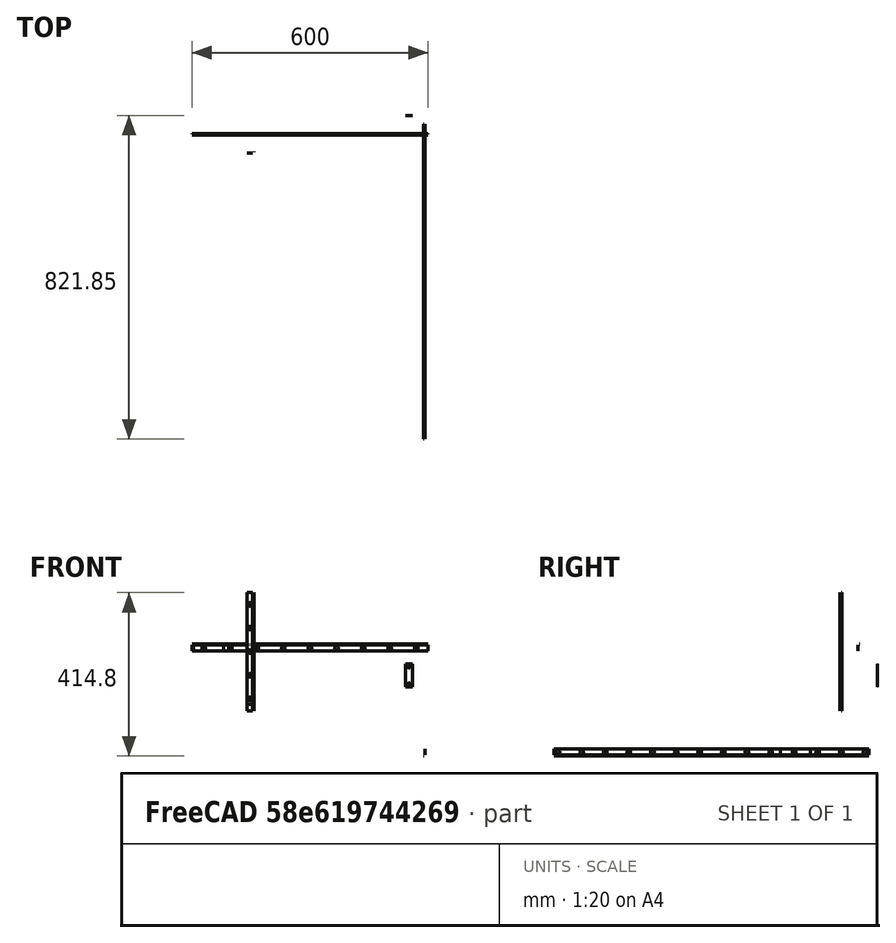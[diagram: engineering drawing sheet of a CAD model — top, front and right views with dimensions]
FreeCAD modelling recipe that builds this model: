
FCSTD DOCUMENT  (FreeCAD 2021.717R24301 +3842 (Git))
Label: 4060CNC
License: Creative Commons Attribution
LicenseURL: http://creativecommons.org/licenses/by/4.0/
objects: App::FeaturePython×31, Part::FeaturePython×21, App::Link×4
note: 20 computed .brp shape members not serialized (recipe doc carries the construction recipe); baked Part::Feature solids carry a one-line shape summary decoded from their .brp
EXTERNAL_REF file=Z-axis.FCStd obj=Assembly
EXTERNAL_REF file=X-axis.FCStd obj=Assembly001
EXTERNAL_REF file=Y-axis.FCStd obj=Assembly
EXTERNAL_REF file=Z-carriage.FCStd obj=Assembly

FEATURE [App::Link] Link  label="Z-axis"
  AutoLinkLabel = true
  AutoPlacement = true
  LinkPlacement = pos=(-190.95,190.1,33.5) rot=(-1e-06,0.707111,-0.707102;0rad)
  LinkedObject = -> <external Z-axis.FCStd>#Assembly
  Placement = pos=(-190.95,190.1,33.5) rot=(-1e-06,0.707111,-0.707102;0rad)
  SyncGroupVisibility = false
  _LinkVersion = 1
FEATURE [App::Link] Link001  label="X-axis"
  AutoLinkLabel = true
  AutoPlacement = true
  LinkPlacement = pos=(15.7,245.5,-55) rot=(0.57735,0.57735,-0.57735;2.0944rad)
  LinkedObject = -> <external X-axis.FCStd>#Assembly001
  Placement = pos=(15.7,245.5,-55) rot=(0.57735,0.57735,-0.57735;2.0944rad)
  SyncGroupVisibility = false
  _LinkVersion = 1
FEATURE [App::Link] Link002  label="Y-axis"
  AutoLinkLabel = true
  AutoPlacement = true
  LinkPlacement = pos=(-233.7,-170,-259.4) rot=(0,0.707107,-0.707107;0rad)
  LinkedObject = -> <external Y-axis.FCStd>#Assembly
  Placement = pos=(-233.7,-170,-259.4) rot=(0,0.707107,-0.707107;0rad)
  SyncGroupVisibility = false
  _LinkVersion = 1
FEATURE [App::Link] Link003  label="Z carriage"
  AutoLinkLabel = true
  AutoPlacement = true
  LinkPlacement = pos=(-278.95,192.85,-22.1) rot=(-5e-06,0.707107,-0.707106;0rad)
  LinkedObject = -> <external Z-carriage.FCStd>#Assembly
  Placement = pos=(-278.95,192.85,-22.1) rot=(-5e-06,0.707107,-0.707106;0rad)
  SyncGroupVisibility = false
  _LinkVersion = 1
FEATURE [Part::FeaturePython] Parts  # WARN: FeaturePython — macro-defined, semantics opaque (R4)
  Group = -> [Link,Link001,Link002,Link003]
  GroupMode = 0
  _LinkVersion = 1
FEATURE [Part::FeaturePython] Assembly  # WARN: FeaturePython — macro-defined, semantics opaque (R4)
  AutoRelax = true
  BuildShape = 0
  Freeze = false
  Group = -> [Constraints,Elements,Parts]
  Verbose = false
  _LinkVersion = 1
  _SolverType = 1
  _Version = 1
FEATURE [App::FeaturePython] Constraints  # WARN: FeaturePython — macro-defined, semantics opaque (R4)
  Group = -> [Constraint001,Constraint002,Constraint003,Constraint004,Constraint005,Constraint,Constraint006,Constraint007,Constraint008,Constraint009]
  _LinkVersion = 1
  _Version = 1
FEATURE [App::FeaturePython] Elements  # WARN: FeaturePython — macro-defined, semantics opaque (R4)
  Group = -> [Element,Element001,Element002,Element003,Element004,Element005,Element006,Element007,Element008,Element009,Element010,Element011,Element012,_Element,_Element001,_Element002,_Element003,_Element004,_Element005]
  _LinkVersion = 1
FEATURE [Part::FeaturePython] Element  label="top-cart-mate@X-axis Assembly"  # link proxy (typed FeaturePython)
  Detach = false
  LinkTransform = true
  LinkedObject = -> Link001 [1.$top-cart-mate@X-beam Assembly.]
  _LinkVersion = 1
  _Parent = -> Elements
FEATURE [Part::FeaturePython] Element001  label="x-top-rail-top-mate@Z-axis assembly"  # link proxy (typed FeaturePython)
  Detach = false
  LinkTransform = true
  LinkedObject = -> Link [1.$x-top-rail-top-mate@HGH20CA-R-Assembly001.]
  _LinkVersion = 1
  _Parent = -> Elements
FEATURE [Part::FeaturePython] Element002  label="x-top-rail-side-mate@Z-axis assembly"  # link proxy (typed FeaturePython)
  Detach = false
  LinkTransform = true
  LinkedObject = -> Link [1.$x-top-rail-side-mate@HGH20CA-R-Assembly001.]
  _LinkVersion = 1
  _Parent = -> Elements
FEATURE [Part::FeaturePython] Element003  label="side-cart-mate@X-axis Assembly"  # link proxy (typed FeaturePython)
  Detach = false
  LinkTransform = true
  LinkedObject = -> Link001 [1.$side-cart-mate@X-beam Assembly.]
  _LinkVersion = 1
  _Parent = -> Elements
FEATURE [App::FeaturePython] Constraint001  label="PlaneAlignment-x-top-rail-cart"  # WARN: FeaturePython — macro-defined, semantics opaque (R4)
  Angle = 0
  AnglePitch = 0
  AngleRoll = 0
  Cascade = false
  Disabled = false
  Group = -> [ElementLink001,ElementLink002]
  LockAngle = false
  _ConstraintType = 37
  _LinkVersion = 1
  _Parent = -> Constraints
FEATURE [App::FeaturePython] ElementLink001  label="top-cart-mate@X-axis Assembly"  # link proxy (typed FeaturePython)
  LinkTransform = true
  LinkedObject = -> Element
  _LinkVersion = 1
  _Parent = -> Constraint001
FEATURE [App::FeaturePython] ElementLink002  label="x-top-rail-top-mate@Z-axis assembly"  # link proxy (typed FeaturePython)
  LinkTransform = true
  LinkedObject = -> Element001
  _LinkVersion = 1
  _Parent = -> Constraint001
FEATURE [App::FeaturePython] Constraint002  label="PlaneAlignment-x-side-rail-cart"  # WARN: FeaturePython — macro-defined, semantics opaque (R4)
  Angle = 0
  AnglePitch = 0
  AngleRoll = 0
  Cascade = false
  Disabled = false
  Group = -> [ElementLink003,ElementLink004]
  LockAngle = false
  _ConstraintType = 37
  _LinkVersion = 1
  _Parent = -> Constraints
FEATURE [App::FeaturePython] ElementLink003  label="side-cart-mate@X-axis Assembly"  # link proxy (typed FeaturePython)
  LinkTransform = true
  LinkedObject = -> Element003
  _LinkVersion = 1
  _Parent = -> Constraint002
FEATURE [App::FeaturePython] ElementLink004  label="x-top-rail-side-mate@Z-axis assembly"  # link proxy (typed FeaturePython)
  LinkTransform = true
  LinkedObject = -> Element002
  _LinkVersion = 1
  _Parent = -> Constraint002
FEATURE [Part::FeaturePython] Element004  label="bf-base@X-axis Assembly"  # link proxy (typed FeaturePython)
  Detach = false
  LinkTransform = true
  LinkedObject = -> Link001 [1.$bf-base@Ballscrew-600-Assembly.]
  _LinkVersion = 1
  _Parent = -> Elements
FEATURE [Part::FeaturePython] Element005  label="x-cart-point@Z-axis assembly"  # link proxy (typed FeaturePython)
  Detach = false
  LinkTransform = true
  LinkedObject = -> Link [1.$x-cart-point@HGH20CA-R-Assembly001.]
  _LinkVersion = 1
  _Parent = -> Elements
FEATURE [Part::FeaturePython] Element006  label="left-point@X-axis Assembly"  # link proxy (typed FeaturePython)
  Detach = false
  LinkTransform = true
  LinkedObject = -> Link001 [1.$left-point@X-beam Assembly.]
  _LinkVersion = 1
  _Parent = -> Elements
FEATURE [App::FeaturePython] Constraint003  label="PointsDistance-X-travel"  # WARN: FeaturePython — macro-defined, semantics opaque (R4)
  Cascade = false
  Disabled = false
  Distance = 80
  Group = -> [ElementLink005,ElementLink006]
  _ConstraintType = 44
  _LinkVersion = 1
  _Parent = -> Constraints
FEATURE [App::FeaturePython] ElementLink005  label="left-point@X-axis Assembly"  # link proxy (typed FeaturePython)
  LinkTransform = true
  LinkedObject = -> Element006
  _LinkVersion = 1
  _Parent = -> Constraint003
FEATURE [App::FeaturePython] ElementLink006  label="x-cart-point@Z-axis assembly"  # link proxy (typed FeaturePython)
  LinkTransform = true
  LinkedObject = -> Element005
  _LinkVersion = 1
  _Parent = -> Constraint003
FEATURE [Part::FeaturePython] Element007  label="top-mate@X-axis Assembly"  # link proxy (typed FeaturePython)
  Detach = false
  LinkTransform = true
  LinkedObject = -> Link001 [1.$top-mate@HGH20CA-R-Assembly.]
  _LinkVersion = 1
  _Parent = -> Elements
FEATURE [Part::FeaturePython] Element008  label="side-mate@X-axis Assembly"  # link proxy (typed FeaturePython)
  Detach = false
  LinkTransform = true
  LinkedObject = -> Link001 [1.$side-mate@HGH20CA-R-Assembly.]
  _LinkVersion = 1
  _Parent = -> Elements
FEATURE [Part::FeaturePython] Element009  label="point@X-axis Assembly"  # link proxy (typed FeaturePython)
  Detach = false
  LinkTransform = true
  LinkedObject = -> Link001 [1.$point@HGH20CA-R-Assembly.]
  _LinkVersion = 1
  _Parent = -> Elements
FEATURE [Part::FeaturePython] Element010  label="side@Base Assembly"  # link proxy (typed FeaturePython)
  Detach = false
  LinkTransform = true
  LinkedObject = -> Link002 [1.$side@HGR20-800 Assembly.]
  _LinkVersion = 1
  _Parent = -> Elements
FEATURE [Part::FeaturePython] Element011  label="point@Base Assembly"  # link proxy (typed FeaturePython)
  Detach = false
  LinkTransform = true
  LinkedObject = -> Link002 [1.$point@HGR20-800 Assembly.]
  _LinkVersion = 1
  _Parent = -> Elements
FEATURE [Part::FeaturePython] Element012  label="top-mate@Base Assembly"  # link proxy (typed FeaturePython)
  Detach = false
  LinkTransform = true
  LinkedObject = -> Link002 [1.$top-mate@HGR20-800 Assembly.]
  _LinkVersion = 1
  _Parent = -> Elements
FEATURE [App::FeaturePython] Constraint004  label="PlaneAlignment-y-top-rail-cart"  # WARN: FeaturePython — macro-defined, semantics opaque (R4)
  Angle = 0
  AnglePitch = 0
  AngleRoll = 0
  Cascade = false
  Disabled = false
  Group = -> [ElementLink007,ElementLink008]
  LockAngle = false
  _ConstraintType = 37
  _LinkVersion = 1
  _Parent = -> Constraints
FEATURE [App::FeaturePython] ElementLink007  label="top-mate@Base Assembly"  # link proxy (typed FeaturePython)
  LinkTransform = true
  LinkedObject = -> Element012
  _LinkVersion = 1
  _Parent = -> Constraint004
FEATURE [App::FeaturePython] ElementLink008  label="top-mate@X-axis Assembly"  # link proxy (typed FeaturePython)
  LinkTransform = true
  LinkedObject = -> Element007
  _LinkVersion = 1
  _Parent = -> Constraint004
FEATURE [App::FeaturePython] Constraint005  label="PlaneAlignment-y-side-rail-cart"  # WARN: FeaturePython — macro-defined, semantics opaque (R4)
  Angle = 0
  AnglePitch = 0
  AngleRoll = 0
  Cascade = false
  Disabled = false
  Group = -> [ElementLink009,ElementLink010]
  LockAngle = false
  _ConstraintType = 37
  _LinkVersion = 1
  _Parent = -> Constraints
FEATURE [App::FeaturePython] ElementLink009  label="side@Base Assembly"  # link proxy (typed FeaturePython)
  LinkTransform = true
  LinkedObject = -> Element010
  _LinkVersion = 1
  _Parent = -> Constraint005
FEATURE [App::FeaturePython] ElementLink010  label="side-mate@X-axis Assembly"  # link proxy (typed FeaturePython)
  LinkTransform = true
  LinkedObject = -> Element008
  _LinkVersion = 1
  _Parent = -> Constraint005
FEATURE [App::FeaturePython] Constraint  label="Locked"  # WARN: FeaturePython — macro-defined, semantics opaque (R4)
  Disabled = false
  Group = -> [ElementLink]
  _ConstraintType = 0
  _LinkVersion = 1
  _Parent = -> Constraints
FEATURE [App::FeaturePython] ElementLink  label="top-mate@Base Assembly"  # link proxy (typed FeaturePython)
  LinkTransform = true
  LinkedObject = -> Element012
  _LinkVersion = 1
  _Parent = -> Constraint
FEATURE [App::FeaturePython] Constraint006  label="PointsDistance-Y-travel"  # WARN: FeaturePython — macro-defined, semantics opaque (R4)
  Cascade = false
  Disabled = false
  Distance = 575
  Group = -> [ElementLink011,ElementLink012]
  _ConstraintType = 44
  _LinkVersion = 1
  _Parent = -> Constraints
FEATURE [App::FeaturePython] ElementLink011  label="point@Base Assembly"  # link proxy (typed FeaturePython)
  LinkTransform = true
  LinkedObject = -> Element011
  _LinkVersion = 1
  _Parent = -> Constraint006
FEATURE [App::FeaturePython] ElementLink012  label="point@X-axis Assembly"  # link proxy (typed FeaturePython)
  LinkTransform = true
  LinkedObject = -> Element009
  _LinkVersion = 1
  _Parent = -> Constraint006
FEATURE [App::FeaturePython] Constraint007  label="PlaneAlignment-z-top-rail-cart"  # WARN: FeaturePython — macro-defined, semantics opaque (R4)
  Angle = 0
  AnglePitch = 0
  AngleRoll = 0
  Cascade = false
  Disabled = false
  Group = -> [ElementLink013,ElementLink014]
  LockAngle = false
  _ConstraintType = 37
  _LinkVersion = 1
  _Parent = -> Constraints
FEATURE [App::FeaturePython] ElementLink013  label="top-mate@Z-axis assembly"  # link proxy (typed FeaturePython)
  LinkTransform = true
  LinkedObject = -> _Element
  _LinkVersion = 1
  _Parent = -> Constraint007
FEATURE [Part::FeaturePython] _Element  label="top-mate@Z-axis assembly"  # link proxy (typed FeaturePython)
  Detach = false
  LinkTransform = true
  LinkedObject = -> Link [1.$top-mate@HGR20-300-Assembly.]
  _LinkVersion = 1
  _Parent = -> Elements
FEATURE [App::FeaturePython] ElementLink014  label="top-mate@Z carriage Assembly"  # link proxy (typed FeaturePython)
  LinkTransform = true
  LinkedObject = -> _Element001
  _LinkVersion = 1
  _Parent = -> Constraint007
FEATURE [Part::FeaturePython] _Element001  label="top-mate@Z carriage Assembly"  # link proxy (typed FeaturePython)
  Detach = false
  LinkTransform = true
  LinkedObject = -> Link003 [1.$top-mate@HGH20CA-R-Assembly.]
  _LinkVersion = 1
  _Parent = -> Elements
FEATURE [App::FeaturePython] Constraint008  label="PlaneAlignment-z-side-rail-cart"  # WARN: FeaturePython — macro-defined, semantics opaque (R4)
  Angle = 0
  AnglePitch = 0
  AngleRoll = 0
  Cascade = false
  Disabled = false
  Group = -> [ElementLink015,ElementLink016]
  LockAngle = false
  _ConstraintType = 37
  _LinkVersion = 1
  _Parent = -> Constraints
FEATURE [App::FeaturePython] ElementLink015  label="r-mate@Z-axis assembly"  # link proxy (typed FeaturePython)
  LinkTransform = true
  LinkedObject = -> _Element002
  _LinkVersion = 1
  _Parent = -> Constraint008
FEATURE [Part::FeaturePython] _Element002  label="r-mate@Z-axis assembly"  # link proxy (typed FeaturePython)
  Detach = false
  LinkTransform = true
  LinkedObject = -> Link [1.$r-mate@HGR20-300-Assembly.]
  _LinkVersion = 1
  _Parent = -> Elements
FEATURE [App::FeaturePython] ElementLink016  label="side-mate@Z carriage Assembly"  # link proxy (typed FeaturePython)
  LinkTransform = true
  LinkedObject = -> _Element003
  _LinkVersion = 1
  _Parent = -> Constraint008
FEATURE [Part::FeaturePython] _Element003  label="side-mate@Z carriage Assembly"  # link proxy (typed FeaturePython)
  Detach = false
  LinkTransform = true
  LinkedObject = -> Link003 [1.$side-mate@HGH20CA-R-Assembly.]
  _LinkVersion = 1
  _Parent = -> Elements
FEATURE [App::FeaturePython] Constraint009  label="PointsDistance-Z-travel"  # WARN: FeaturePython — macro-defined, semantics opaque (R4)
  Cascade = false
  Disabled = false
  Distance = 16
  Group = -> [ElementLink017,ElementLink018]
  _ConstraintType = 44
  _LinkVersion = 1
  _Parent = -> Constraints
FEATURE [App::FeaturePython] ElementLink017  label="point@Z-axis assembly"  # link proxy (typed FeaturePython)
  LinkTransform = true
  LinkedObject = -> _Element004
  _LinkVersion = 1
  _Parent = -> Constraint009
FEATURE [Part::FeaturePython] _Element004  label="point@Z-axis assembly"  # link proxy (typed FeaturePython)
  Detach = false
  LinkTransform = true
  LinkedObject = -> Link [1.$point@HGR20-300-Assembly.]
  _LinkVersion = 1
  _Parent = -> Elements
FEATURE [App::FeaturePython] ElementLink018  label="point@Z carriage Assembly"  # link proxy (typed FeaturePython)
  LinkTransform = true
  LinkedObject = -> _Element005
  _LinkVersion = 1
  _Parent = -> Constraint009
FEATURE [Part::FeaturePython] _Element005  label="point@Z carriage Assembly"  # link proxy (typed FeaturePython)
  Detach = false
  LinkTransform = true
  LinkedObject = -> Link003 [1.$point@HGH20CA-R-Assembly.]
  _LinkVersion = 1
  _Parent = -> Elements

RESOLVED EXTERNAL PARTS (link-assembly join: the EXTERNAL_REF files above that resolve inside this repo's crawl, each included once):
---- part X-axis.FCStd = doc fcstd_a2c1d80cc1b0 ----
FCSTD DOCUMENT  (FreeCAD 2021.717R24301 +3842 (Git))
Label: X-axis
License: Creative Commons Attribution
LicenseURL: http://creativecommons.org/licenses/by/4.0/
objects: App::FeaturePython×78, Part::FeaturePython×72, App::Link×20, App::LinkElement×4, App::DocumentObjectGroup×1
note: 69 computed .brp shape members not serialized (recipe doc carries the construction recipe); baked Part::Feature solids carry a one-line shape summary decoded from their .brp
EXTERNAL_REF file=parts/HGR20.FCStd obj=Assembly001
EXTERNAL_REF file=parts/X axis plates.FCStd obj=Assembly001
EXTERNAL_REF file=parts/X axis plates.FCStd obj=Assembly
EXTERNAL_REF file=parts/Ballscrew.FCStd obj=Assembly003
EXTERNAL_REF file=parts/NEMA23-76.FCStd obj=Assembly001
EXTERNAL_REF file=parts/NEMA23-76.FCStd obj=Assembly
EXTERNAL_REF file=parts/X axis plates.FCStd obj=Assembly003
EXTERNAL_REF file=parts/HGH20CA.FCStd obj=Assembly
EXTERNAL_REF file=parts/HGH20CA.FCStd obj=Assembly001
EXTERNAL_REF file=parts/BallNut.FCStd obj=Assembly
EXTERNAL_REF file=parts/X axis plates.FCStd obj=Assembly005
EXTERNAL_REF file=parts/Extrusion.FCStd obj=Body001
EXTERNAL_REF file=parts/LimitSensor.FCStd obj=Assembly

FEATURE [App::Link] Link  label="HGR20-600"
  AutoLinkLabel = true
  AutoPlacement = true
  LinkPlacement = pos=(-97.7,1.41e-14,25.4) rot=(0,0,1;0rad)
  LinkedObject = -> <external parts/HGR20.FCStd>#Assembly001
  Placement = pos=(-97.7,1.41e-14,25.4) rot=(0,0,1;0rad)
  SyncGroupVisibility = false
  _LinkVersion = 1
FEATURE [App::Link] Link002  label="Top beam"
  AutoLinkLabel = true
  AutoPlacement = true
  LinkedObject = -> Assembly
  SyncGroupVisibility = false
  _LinkVersion = 1
FEATURE [App::Link] Link003  label="Bottom beam"
  AutoLinkLabel = true
  AutoPlacement = true
  LinkPlacement = pos=(-55.7,-2.274e-13,1.776e-13) rot=(0,0,-1;3.14159rad)
  LinkedObject = -> Assembly
  Placement = pos=(-55.7,-2.274e-13,1.776e-13) rot=(0,0,-1;3.14159rad)
  SyncGroupVisibility = false
  _LinkVersion = 1
FEATURE [App::Link] Link004  label="Left plate"
  AutoLinkLabel = true
  AutoPlacement = true
  LinkPlacement = pos=(166.3,-323.85,58.6) rot=(0,1,0;4.71239rad)
  LinkedObject = -> <external parts/X axis plates.FCStd>#Assembly001
  Placement = pos=(166.3,-323.85,58.6) rot=(0,1,0;4.71239rad)
  SyncGroupVisibility = false
  _LinkVersion = 1
FEATURE [App::Link] Link005  label="Right plate"
  AutoLinkLabel = true
  AutoPlacement = true
  LinkPlacement = pos=(166.3,69.85,58.6) rot=(0,1,0;4.71239rad)
  LinkedObject = -> <external parts/X axis plates.FCStd>#Assembly
  Placement = pos=(166.3,69.85,58.6) rot=(0,1,0;4.71239rad)
  SyncGroupVisibility = false
  _LinkVersion = 1
FEATURE [App::Link] Link006  label="Ballscrew-600"
  AutoLinkLabel = true
  AutoPlacement = true
  LinkPlacement = pos=(-27.85,251.9,-6.35) rot=(0,0,-1;3.14159rad)
  LinkedObject = -> <external parts/Ballscrew.FCStd>#Assembly003
  Placement = pos=(-27.85,251.9,-6.35) rot=(0,0,-1;3.14159rad)
  SyncGroupVisibility = false
  _LinkVersion = 1
FEATURE [App::Link] Link007  label="Coupling"
  AutoLinkLabel = true
  AutoPlacement = true
  LinkPlacement = pos=(-27.85,-296.25,18.65) rot=(-0.57735,-0.57735,-0.57735;2.0944rad)
  LinkedObject = -> <external parts/NEMA23-76.FCStd>#Assembly001
  Placement = pos=(-27.85,-296.25,18.65) rot=(-0.57735,-0.57735,-0.57735;2.0944rad)
  SyncGroupVisibility = false
  _LinkVersion = 1
FEATURE [App::Link] Link008  label="NEMA23-76"
  AutoLinkLabel = true
  AutoPlacement = true
  LinkPlacement = pos=(-27.85,-323.85,18.65) rot=(0.57735,-0.57735,0.57735;2.0944rad)
  LinkedObject = -> <external parts/NEMA23-76.FCStd>#Assembly
  Placement = pos=(-27.85,-323.85,18.65) rot=(0.57735,-0.57735,0.57735;2.0944rad)
  SyncGroupVisibility = false
  _LinkVersion = 1
FEATURE [App::Link] Link009  label="Rear plate"
  AutoLinkLabel = true
  AutoPlacement = true
  LinkPlacement = pos=(209.15,-76,-12.7) rot=(0,1,0;4.71239rad)
  LinkedObject = -> <external parts/X axis plates.FCStd>#Assembly003
  Placement = pos=(209.15,-76,-12.7) rot=(0,1,0;4.71239rad)
  SyncGroupVisibility = false
  _LinkVersion = 1
FEATURE [App::Link] Link012  label="HGH20CA-L-L"
  AutoLinkLabel = true
  AutoPlacement = true
  LinkPlacement = pos=(166.3,-274.8,202.6) rot=(-1,0,0;4.71239rad)
  LinkedObject = -> <external parts/HGH20CA.FCStd>#Assembly
  Placement = pos=(166.3,-274.8,202.6) rot=(-1,0,0;4.71239rad)
  SyncGroupVisibility = false
  _LinkVersion = 1
FEATURE [App::Link] Link013  label="HGH20CA-L-R"
  AutoLinkLabel = true
  AutoPlacement = true
  LinkPlacement = pos=(166.3,-274.8,58.6) rot=(-1,0,0;4.71239rad)
  LinkedObject = -> <external parts/HGH20CA.FCStd>#Assembly001
  Placement = pos=(166.3,-274.8,58.6) rot=(-1,0,0;4.71239rad)
  SyncGroupVisibility = false
  _LinkVersion = 1
FEATURE [App::Link] Link014  label="HGH20CA-R-L"
  AutoLinkLabel = true
  AutoPlacement = true
  LinkPlacement = pos=(166.3,274.8,58.6) rot=(1,0,0;4.71239rad)
  LinkedObject = -> Link012
  Placement = pos=(166.3,274.8,58.6) rot=(1,0,0;4.71239rad)
  SyncGroupVisibility = false
  _LinkVersion = 1
FEATURE [App::Link] Link015  label="HGH20CA-R-R"
  AutoLinkLabel = true
  AutoPlacement = true
  LinkPlacement = pos=(166.3,274.8,202.6) rot=(1,0,0;4.71239rad)
  LinkedObject = -> Link013
  Placement = pos=(166.3,274.8,202.6) rot=(1,0,0;4.71239rad)
  SyncGroupVisibility = false
  _LinkVersion = 1
FEATURE [App::Link] Link020  label="Left nut"
  AutoLinkLabel = true
  AutoPlacement = true
  LinkPlacement = pos=(219.3,-305.675,131.475) rot=(0,0.707107,0.707107;3.14159rad)
  LinkedObject = -> <external parts/BallNut.FCStd>#Assembly
  Placement = pos=(219.3,-305.675,131.475) rot=(0,0.707107,0.707107;3.14159rad)
  SyncGroupVisibility = false
  _LinkVersion = 1
FEATURE [App::Link] Link021  label="Right nut"
  AutoLinkLabel = true
  AutoPlacement = true
  LinkPlacement = pos=(219.3,305.675,131.475) rot=(1,0,0;1.5708rad)
  LinkedObject = -> <external parts/BallNut.FCStd>#Assembly
  Placement = pos=(219.3,305.675,131.475) rot=(1,0,0;1.5708rad)
  SyncGroupVisibility = false
  _LinkVersion = 1
FEATURE [App::Link] Link022  label="Gouverner left"
  AutoLinkLabel = true
  AutoPlacement = true
  LinkPlacement = pos=(166.3,-323.85,130.6) rot=(0,1,0;4.71239rad)
  LinkedObject = -> <external parts/X axis plates.FCStd>#Assembly005
  Placement = pos=(166.3,-323.85,130.6) rot=(0,1,0;4.71239rad)
  SyncGroupVisibility = false
  _LinkVersion = 1
FEATURE [App::Link] Link023  label="Gouverner right"
  AutoLinkLabel = true
  AutoPlacement = true
  LinkPlacement = pos=(166.3,323.85,130.6) rot=(0.707107,0,-0.707107;3.14159rad)
  LinkedObject = -> <external parts/X axis plates.FCStd>#Assembly005
  Placement = pos=(166.3,323.85,130.6) rot=(0.707107,0,-0.707107;3.14159rad)
  SyncGroupVisibility = false
  _LinkVersion = 1
FEATURE [App::Link] Link024  label="Extrusion"
  AutoLinkLabel = true
  AutoPlacement = true
  LinkPlacement = pos=(-85,0,0) rot=(0,0,1;0rad)
  LinkedObject = -> <external parts/Extrusion.FCStd>#Body001
  Placement = pos=(-85,0,0) rot=(0,0,1;0rad)
  SyncGroupVisibility = false
  _LinkVersion = 1
FEATURE [Part::FeaturePython] Washer  label="1/4in-Washer"  # Fasteners workbench fastener (typed FeaturePython)
  Placement = pos=(0,0,-1.6002) rot=(0,0,1;0rad)
  diameter = 11
  invert = false
  matchOuter = false
  offset = 0
  type = 1
FEATURE [Part::FeaturePython] Screw  label="1/4inx1/2in-Screw"  # Fasteners workbench fastener (typed FeaturePython)
  diameter = 11
  invert = false
  length = 4
  lengthCustom = 12.7
  matchOuter = false
  offset = 0
  thread = false
  type = 4
FEATURE [Part::FeaturePython] Parts002  # WARN: FeaturePython — macro-defined, semantics opaque (R4)
  Group = -> [Washer,Screw]
  GroupMode = 0
  _LinkVersion = 1
FEATURE [App::LinkElement] Link025_i0
  LinkPlacement = pos=(-63.4102,-234.8,-12.7) rot=(-0.57735,-0.57735,0.57735;2.0944rad)
  LinkedObject = -> Assembly002
  Placement = pos=(-63.4102,-234.8,-12.7) rot=(-0.57735,-0.57735,0.57735;2.0944rad)
  _LinkVersion = 1
FEATURE [App::LinkElement] Link025_i1
  LinkPlacement = pos=(-63.4102,-78.2667,-12.7) rot=(-0.57735,-0.57735,0.57735;2.0944rad)
  LinkedObject = -> Assembly002
  Placement = pos=(-63.4102,-78.2667,-12.7) rot=(-0.57735,-0.57735,0.57735;2.0944rad)
  _LinkVersion = 1
FEATURE [App::LinkElement] Link025_i2
  LinkPlacement = pos=(-63.4102,78.2667,-12.7) rot=(-0.57735,-0.57735,0.57735;2.0944rad)
  LinkedObject = -> Assembly002
  Placement = pos=(-63.4102,78.2667,-12.7) rot=(-0.57735,-0.57735,0.57735;2.0944rad)
  _LinkVersion = 1
FEATURE [App::LinkElement] Link025_i3
  LinkPlacement = pos=(-63.4102,234.8,-12.7) rot=(-0.57735,-0.57735,0.57735;2.0944rad)
  LinkedObject = -> Assembly002
  Placement = pos=(-63.4102,234.8,-12.7) rot=(-0.57735,-0.57735,0.57735;2.0944rad)
  _LinkVersion = 1
FEATURE [App::Link] Link025  label="1/4x1/2 screw and washer Assembly 4ct"
  AutoLinkLabel = true
  AutoPlacement = true
  ElementCount = 4
  ElementList = -> [Link025_i0,Link025_i1,Link025_i2,Link025_i3]
  LinkedObject = -> Assembly002
  SyncGroupVisibility = false
  _LinkVersion = 1
FEATURE [Part::FeaturePython] Parts  # WARN: FeaturePython — macro-defined, semantics opaque (R4)
  Group = -> [Link,Link024,Link025]
  GroupMode = 0
  _LinkVersion = 1
FEATURE [App::Link] Link026  label="Limit sensor"
  AutoLinkLabel = true
  AutoPlacement = true
  LinkPlacement = pos=(-62.4,-304.8,56.1) rot=(-1,0,0;3.14159rad)
  LinkedObject = -> <external parts/LimitSensor.FCStd>#Assembly
  Placement = pos=(-62.4,-304.8,56.1) rot=(-1,0,0;3.14159rad)
  SyncGroupVisibility = false
  _LinkVersion = 1
FEATURE [Part::FeaturePython] Parts001  # WARN: FeaturePython — macro-defined, semantics opaque (R4)
  Group = -> [Link002,Link003,Link004,Link005,Link006,Link007,Link008,Link009,Link012,Link013,Link014,Link015,Link020,Link021,Link022,Link023,Link026]
  GroupMode = 0
  _LinkVersion = 1
FEATURE [Part::FeaturePython] Assembly  label="X-beam Assembly"  # WARN: FeaturePython — macro-defined, semantics opaque (R4)
  AutoRelax = true
  BuildShape = 0
  Freeze = false
  Group = -> [Constraints,Elements,Parts]
  Verbose = false
  _LinkVersion = 1
  _SolverType = 1
  _Version = 1
FEATURE [App::FeaturePython] Constraints  # WARN: FeaturePython — macro-defined, semantics opaque (R4)
  Group = -> [Constraint,Constraint001,Constraint032,Constraint033,Constraint034,Constraint035]
  _LinkVersion = 1
  _Version = 1
FEATURE [App::FeaturePython] Elements  # WARN: FeaturePython — macro-defined, semantics opaque (R4)
  Group = -> [Element,Element001,Element002,Element003,Element007,Element008,Element012,Element013,_Element002,_Element003,_Element004,_Element005,_Element006,_Element007,_Element008,_Element009]
  _LinkVersion = 1
FEATURE [Part::FeaturePython] Element  label="center-mate@HGR20-600-Assembly"  # link proxy (typed FeaturePython)
  Detach = false
  LinkTransform = true
  LinkedObject = -> Link [1.$center-mate.]
  _LinkVersion = 1
  _Parent = -> Elements
FEATURE [Part::FeaturePython] Element001  label="extrusion center"  # link proxy (typed FeaturePython)
  Detach = false
  LinkTransform = true
  LinkedObject = -> Link024 [Sketch001.]
  _LinkVersion = 1
  _Parent = -> Elements
FEATURE [App::FeaturePython] Constraint  label="Locked"  # WARN: FeaturePython — macro-defined, semantics opaque (R4)
  Disabled = false
  Group = -> [ElementLink]
  _ConstraintType = 0
  _LinkVersion = 1
  _Parent = -> Constraints
FEATURE [App::FeaturePython] ElementLink  label="extrusion center"  # link proxy (typed FeaturePython)
  LinkTransform = true
  LinkedObject = -> Element001
  _LinkVersion = 1
  _Parent = -> Constraint
FEATURE [App::FeaturePython] Constraint001  label="Attachment"  # WARN: FeaturePython — macro-defined, semantics opaque (R4)
  Cascade = false
  Disabled = false
  Group = -> [ElementLink001,ElementLink002]
  Multiply = false
  _ConstraintType = 45
  _LinkVersion = 1
  _Parent = -> Constraints
FEATURE [App::FeaturePython] ElementLink001  label="extrusion center"  # link proxy (typed FeaturePython)
  LinkTransform = true
  LinkedObject = -> Element001
  _LinkVersion = 1
  _Parent = -> Constraint001
FEATURE [App::FeaturePython] ElementLink002  label="center-mate@HGR20-600-Assembly"  # link proxy (typed FeaturePython)
  LinkTransform = true
  LinkedObject = -> Element
  Offset = pos=(0,0,0) rot=(1,0,0;3.14159rad)
  Placement = pos=(1.42e-14,3.13e-14,50.8) rot=(1,0,0;3.14159rad)
  _LinkVersion = 1
  _Parent = -> Constraint001
FEATURE [Part::FeaturePython] Element002  label="top-cart-mate"  # link proxy (typed FeaturePython)
  Detach = false
  LinkTransform = true
  LinkedObject = -> Link [1.$top-mate.]
  _LinkVersion = 1
  _Parent = -> Elements
FEATURE [Part::FeaturePython] Element003  label="side-cart-mate"  # link proxy (typed FeaturePython)
  Detach = false
  LinkTransform = true
  LinkedObject = -> Link [1.$side-mate.]
  _LinkVersion = 1
  _Parent = -> Elements
FEATURE [Part::FeaturePython] Assembly001  label="X-axis Assembly"  # WARN: FeaturePython — macro-defined, semantics opaque (R4)
  AutoRelax = true
  BuildShape = 0
  Freeze = false
  Group = -> [Constraints001,Elements001,Parts001]
  Placement = pos=(79.15,3.69183,42.8418) rot=(-0.57735,-0.57735,0.57735;4.18879rad)
  Verbose = false
  _LinkVersion = 1
  _SolverType = 1
  _Version = 1
FEATURE [App::FeaturePython] Constraints001  # WARN: FeaturePython — macro-defined, semantics opaque (R4)
  Group = -> [Constraint002,Constraint003,Constraint004,Constraint005,Constraint011,Constraint012,Constraint013,Constraint021,Constraint022,Constraint023,Constraint024,Constraint025,Constraint026,Constraint027,Constraint028,Constraint029,Constraint036]
  _LinkVersion = 1
  _Version = 1
FEATURE [App::FeaturePython] Elements001  # WARN: FeaturePython — macro-defined, semantics opaque (R4)
  Group = -> [Element004,Element005,Element006,Element009,Element010,Element011,Element014,Element015,Element016,Element017,Element018,Element019,Element020,Element021,Element022,Element023,Element024,Element025,Element026,Element027,Element028,Element030,Element031,Element034,Element036,Element038,Element040,Element046,Element047,Element048,Element049,Element054,Element055,Element056,Element057,Element058,+9 more]
  _LinkVersion = 1
FEATURE [Part::FeaturePython] Element004  label="top-cart-mate@X-beam Assembly"  # link proxy (typed FeaturePython)
  Detach = false
  LinkTransform = true
  LinkedObject = -> Link002 [1.$top-cart-mate.]
  _LinkVersion = 1
  _Parent = -> Elements001
FEATURE [Part::FeaturePython] Element005  label="side-cart-mate@X-beam Assembly"  # link proxy (typed FeaturePython)
  Detach = false
  LinkTransform = true
  LinkedObject = -> Link002 [1.$side-cart-mate.]
  _LinkVersion = 1
  _Parent = -> Elements001
FEATURE [Part::FeaturePython] Element006  label="extrusion center@X-beam Assembly"  # link proxy (typed FeaturePython)
  Detach = false
  LinkTransform = true
  LinkedObject = -> Link002 [1.$extrusion center.]
  _LinkVersion = 1
  _Parent = -> Elements001
FEATURE [App::FeaturePython] Constraint002  label="Locked001"  # WARN: FeaturePython — macro-defined, semantics opaque (R4)
  Disabled = false
  Group = -> [ElementLink003]
  _ConstraintType = 0
  _LinkVersion = 1
  _Parent = -> Constraints001
FEATURE [App::FeaturePython] ElementLink003  label="extrusion center@X-beam Assembly"  # link proxy (typed FeaturePython)
  LinkTransform = true
  LinkedObject = -> Element006
  _LinkVersion = 1
  _Parent = -> Constraint002
FEATURE [Part::FeaturePython] Element007  label="left-point@HGR20-600-Assembly"  # link proxy (typed FeaturePython)
  Detach = false
  LinkTransform = true
  LinkedObject = -> Link [1.$left-point.]
  _LinkVersion = 1
  _Parent = -> Elements
FEATURE [Part::FeaturePython] Element008  label="right-point@HGR20-600-Assembly"  # link proxy (typed FeaturePython)
  Detach = false
  LinkTransform = true
  LinkedObject = -> Link [1.$right-point.]
  _LinkVersion = 1
  _Parent = -> Elements
FEATURE [Part::FeaturePython] Element009  label="left-point@X-beam Assembly"  # link proxy (typed FeaturePython)
  Detach = false
  LinkTransform = true
  LinkedObject = -> Link002 [1.$left-point@HGR20-600-Assembly.]
  _LinkVersion = 1
  _Parent = -> Elements001
FEATURE [Part::FeaturePython] Element010  label="right-point@X-beam Assembly"  # link proxy (typed FeaturePython)
  Detach = false
  LinkTransform = true
  LinkedObject = -> Link003 [1.$right-point@HGR20-600-Assembly.]
  _LinkVersion = 1
  _Parent = -> Elements001
FEATURE [Part::FeaturePython] Element011  label="side-cart-mate@X-beam Assembly001"  # link proxy (typed FeaturePython)
  Detach = false
  LinkTransform = true
  LinkedObject = -> Link003 [1.$side-cart-mate.]
  _LinkVersion = 1
  _Parent = -> Elements001
FEATURE [Part::FeaturePython] Element012  label="plate-mate-1"  # link proxy (typed FeaturePython)
  Detach = false
  LinkTransform = true
  LinkedObject = -> Link024 [Pocket004.Edge345]
  _LinkVersion = 1
  _Parent = -> Elements
FEATURE [Part::FeaturePython] Element013  label="plate-mate-2"  # link proxy (typed FeaturePython)
  Detach = false
  LinkTransform = true
  LinkedObject = -> Link024 [Pocket004.Edge176]
  _LinkVersion = 1
  _Parent = -> Elements
FEATURE [Part::FeaturePython] Element014  label="plate-mate-tl@X-beam Assembly"  # link proxy (typed FeaturePython)
  Detach = false
  LinkTransform = true
  LinkedObject = -> Link002 [1.$plate-mate-1.]
  _LinkVersion = 1
  _Parent = -> Elements001
FEATURE [Part::FeaturePython] Element015  label="plate-mate-tr@X-beam Assembly"  # link proxy (typed FeaturePython)
  Detach = false
  LinkTransform = true
  LinkedObject = -> Link002 [1.$plate-mate-2.]
  _LinkVersion = 1
  _Parent = -> Elements001
FEATURE [Part::FeaturePython] Element016  label="plate-mate-br@X-beam Assembly"  # link proxy (typed FeaturePython)
  Detach = false
  LinkTransform = true
  LinkedObject = -> Link003 [1.$plate-mate-1.]
  _LinkVersion = 1
  _Parent = -> Elements001
FEATURE [Part::FeaturePython] Element017  label="plate-mate-bl@X-beam Assembly"  # link proxy (typed FeaturePython)
  Detach = false
  LinkTransform = true
  LinkedObject = -> Link003 [1.$plate-mate-2.]
  _LinkVersion = 1
  _Parent = -> Elements001
FEATURE [Part::FeaturePython] Element018  label="bottom-beam-mate@Left plate Assembly"  # link proxy (typed FeaturePython)
  Detach = false
  LinkTransform = true
  LinkedObject = -> Link004 [1.$bottom-beam-mate.]
  _LinkVersion = 1
  _Parent = -> Elements001
FEATURE [Part::FeaturePython] Element019  label="top-beam-mate@Left plate Assembly"  # link proxy (typed FeaturePython)
  Detach = false
  LinkTransform = true
  LinkedObject = -> Link004 [1.$top-beam-mate.]
  _LinkVersion = 1
  _Parent = -> Elements001
FEATURE [Part::FeaturePython] Element020  label="top-beam-mate@Right plate Assembly"  # link proxy (typed FeaturePython)
  Detach = false
  LinkTransform = true
  LinkedObject = -> Link005 [1.$top-beam-mate.]
  _LinkVersion = 1
  _Parent = -> Elements001
FEATURE [App::FeaturePython] Constraint003  label="Attachment-beam-tr"  # WARN: FeaturePython — macro-defined, semantics opaque (R4)
  Cascade = false
  Disabled = false
  Group = -> [ElementLink004,ElementLink005]
  Multiply = false
  _ConstraintType = 45
  _LinkVersion = 1
  _Parent = -> Constraints001
FEATURE [App::FeaturePython] ElementLink004  label="_top-beam-mate@Right plate Assembly"  # link proxy (typed FeaturePython)
  LinkTransform = true
  LinkedObject = -> _Element010
  _LinkVersion = 1
  _Parent = -> Constraint003
FEATURE [App::FeaturePython] ElementLink005  label="plate-mate-tr@X-beam Assembly"  # link proxy (typed FeaturePython)
  LinkTransform = true
  LinkedObject = -> Element015
  Offset = pos=(0,0,0) rot=(0,0,1;1.5708rad)
  Placement = pos=(-110.4,0,85) rot=(0,-1,0;1.5708rad)
  _LinkVersion = 1
  _Parent = -> Constraint003
FEATURE [App::FeaturePython] Constraint004  label="Attachment-beam-tl"  # WARN: FeaturePython — macro-defined, semantics opaque (R4)
  Cascade = false
  Disabled = false
  Group = -> [ElementLink006,ElementLink007]
  Multiply = false
  _ConstraintType = 45
  _LinkVersion = 1
  _Parent = -> Constraints001
FEATURE [App::FeaturePython] ElementLink006  label="top-beam-mate@Left plate Assembly"  # link proxy (typed FeaturePython)
  LinkTransform = true
  LinkedObject = -> Element019
  _LinkVersion = 1
  _Parent = -> Constraint004
FEATURE [App::FeaturePython] ElementLink007  label="plate-mate-tl@X-beam Assembly"  # link proxy (typed FeaturePython)
  LinkTransform = true
  LinkedObject = -> Element014
  Offset = pos=(0,0,0) rot=(0,0,1;1.5708rad)
  Placement = pos=(-110.4,0,85) rot=(0,-1,0;1.5708rad)
  _LinkVersion = 1
  _Parent = -> Constraint004
FEATURE [App::FeaturePython] Constraint005  label="Attachment-beam-bl"  # WARN: FeaturePython — macro-defined, semantics opaque (R4)
  Cascade = false
  Disabled = false
  Group = -> [ElementLink008,ElementLink009]
  Multiply = false
  _ConstraintType = 45
  _LinkVersion = 1
  _Parent = -> Constraints001
FEATURE [App::FeaturePython] ElementLink008  label="bottom-beam-mate@Left plate Assembly"  # link proxy (typed FeaturePython)
  LinkTransform = true
  LinkedObject = -> Element018
  Offset = pos=(0,0,0) rot=(0,0,1;1.5708rad)
  Placement = pos=(29.3,0,-54.7) rot=(0,-1,0;1.5708rad)
  _LinkVersion = 1
  _Parent = -> Constraint005
FEATURE [App::FeaturePython] ElementLink009  label="plate-mate-bl@X-beam Assembly"  # link proxy (typed FeaturePython)
  LinkTransform = true
  LinkedObject = -> Element017
  Offset = pos=(0,0,0) rot=(1,0,0;3.14159rad)
  Placement = pos=(-8.53e-14,-609.6,-25.4) rot=(1,0,0;3.14159rad)
  _LinkVersion = 1
  _Parent = -> Constraint005
FEATURE [Part::FeaturePython] Element021  label="screw-mate@Coupling-Assembly"  # link proxy (typed FeaturePython)
  Detach = false
  LinkTransform = true
  LinkedObject = -> Link007 [1.$screw-mate.]
  _LinkVersion = 1
  _Parent = -> Elements001
FEATURE [Part::FeaturePython] Element022  label="coupling-mate@Ballscrew-600-Assembly"  # link proxy (typed FeaturePython)
  Detach = false
  LinkTransform = true
  LinkedObject = -> Link006 [1.$coupling-mate.]
  _LinkVersion = 1
  _Parent = -> Elements001
FEATURE [Part::FeaturePython] Element023  label="motor-mate@Coupling-Assembly"  # link proxy (typed FeaturePython)
  Detach = false
  LinkTransform = true
  LinkedObject = -> Link007 [1.$motor-mate.]
  _LinkVersion = 1
  _Parent = -> Elements001
FEATURE [Part::FeaturePython] Element024  label="coupling-mate@NEMA23-76-Assembly"  # link proxy (typed FeaturePython)
  Detach = false
  LinkTransform = true
  LinkedObject = -> Link008 [1.$coupling-mate.]
  _LinkVersion = 1
  _Parent = -> Elements001
FEATURE [Part::FeaturePython] Element025  label="plate-mate@NEMA23-76-Assembly"  # link proxy (typed FeaturePython)
  Detach = false
  LinkTransform = true
  LinkedObject = -> Link008 [1.$bracket-mate.]
  _LinkVersion = 1
  _Parent = -> Elements001
FEATURE [Part::FeaturePython] Element026  label="motor-mate@Left plate Assembly"  # link proxy (typed FeaturePython)
  Detach = false
  LinkTransform = true
  LinkedObject = -> Link004 [1.$motor-mate.]
  _LinkVersion = 1
  _Parent = -> Elements001
FEATURE [Part::FeaturePython] Element027  label="bf-base@Ballscrew-600-Assembly"  # link proxy (typed FeaturePython)
  Detach = false
  LinkTransform = true
  LinkedObject = -> Link006 [1.$bf-base.]
  _LinkVersion = 1
  _Parent = -> Elements001
FEATURE [App::FeaturePython] Constraint011  label="Attachment-motor-coupling"  # WARN: FeaturePython — macro-defined, semantics opaque (R4)
  Cascade = false
  Disabled = false
  Group = -> [ElementLink019,ElementLink020]
  Multiply = false
  _ConstraintType = 45
  _LinkVersion = 1
  _Parent = -> Constraints001
FEATURE [App::FeaturePython] ElementLink019  label="coupling-mate@NEMA23-76-Assembly"  # link proxy (typed FeaturePython)
  LinkTransform = true
  LinkedObject = -> Element024
  _LinkVersion = 1
  _Parent = -> Constraint011
FEATURE [App::FeaturePython] ElementLink020  label="motor-mate@Coupling-Assembly"  # link proxy (typed FeaturePython)
  LinkTransform = true
  LinkedObject = -> Element023
  _LinkVersion = 1
  _Parent = -> Constraint011
FEATURE [App::FeaturePython] Constraint012  label="Attachment-screw-coupling"  # WARN: FeaturePython — macro-defined, semantics opaque (R4)
  Cascade = false
  Disabled = false
  Group = -> [ElementLink021,ElementLink022]
  Multiply = false
  _ConstraintType = 45
  _LinkVersion = 1
  _Parent = -> Constraints001
FEATURE [App::FeaturePython] ElementLink021  label="coupling-mate@Ballscrew-600-Assembly"  # link proxy (typed FeaturePython)
  LinkTransform = true
  LinkedObject = -> Element022
  Offset = pos=(0,0,0) rot=(1,0,0;3.14159rad)
  Placement = pos=(1.51559e-11,-582.5,37.3) rot=(1,0,0;3.14159rad)
  _LinkVersion = 1
  _Parent = -> Constraint012
FEATURE [App::FeaturePython] ElementLink022  label="screw-mate@Coupling-Assembly"  # link proxy (typed FeaturePython)
  LinkTransform = true
  LinkedObject = -> Element021
  Offset = pos=(0,0,0) rot=(0,0,1;4.71239rad)
  Placement = pos=(-9.2,1.53936e-08,46.5) rot=(0,-1,0;1.5708rad)
  _LinkVersion = 1
  _Parent = -> Constraint012
FEATURE [Part::FeaturePython] Element028  label="side-mate@Rear plate left Assembly"  # link proxy (typed FeaturePython)
  Detach = false
  LinkTransform = true
  LinkedObject = -> Link009 [1.$side-mate-L.]
  _LinkVersion = 1
  _Parent = -> Elements001
FEATURE [Part::FeaturePython] Element030  label="rear-mate@Left plate Assembly"  # link proxy (typed FeaturePython)
  Detach = false
  LinkTransform = true
  LinkedObject = -> Link004 [1.$rear-mate.]
  _LinkVersion = 1
  _Parent = -> Elements001
FEATURE [Part::FeaturePython] Element031  label="rear-mate@Right plate Assembly"  # link proxy (typed FeaturePython)
  Detach = false
  LinkTransform = true
  LinkedObject = -> Link005 [1.$rear-mate.]
  _LinkVersion = 1
  _Parent = -> Elements001
FEATURE [App::FeaturePython] Constraint013  label="Attachment-left-rear"  # WARN: FeaturePython — macro-defined, semantics opaque (R4)
  Cascade = false
  Disabled = false
  Group = -> [ElementLink023,ElementLink024]
  Multiply = false
  _ConstraintType = 45
  _LinkVersion = 1
  _Parent = -> Constraints001
FEATURE [App::FeaturePython] ElementLink023  label="rear-mate@Left plate Assembly"  # link proxy (typed FeaturePython)
  LinkTransform = true
  LinkedObject = -> Element030
  Offset = pos=(0,0,0) rot=(1,0,0;3.14159rad)
  Placement = pos=(-55.7,-609.6,-1.634e-13) rot=(0,0,1;3.14159rad)
  _LinkVersion = 1
  _Parent = -> Constraint013
FEATURE [App::FeaturePython] ElementLink024  label="side-mate@Rear plate left Assembly"  # link proxy (typed FeaturePython)
  LinkTransform = true
  LinkedObject = -> Element028
  Offset = pos=(0,0,0) rot=(0,0,1;1.5708rad)
  Placement = pos=(-40.55,5.68e-14,15.15) rot=(0,-1,0;1.5708rad)
  _LinkVersion = 1
  _Parent = -> Constraint013
FEATURE [Part::FeaturePython] Element034  label="shim-L-L@HGH20CA-L-Assembly"  # link proxy (typed FeaturePython)
  Detach = false
  LinkTransform = true
  LinkedObject = -> Link012 [1.$shim-tr.]
  _LinkVersion = 1
  _Parent = -> Elements001
FEATURE [Part::FeaturePython] Element036  label="shim-L-R@HGH20CA-R-Assembly"  # link proxy (typed FeaturePython)
  Detach = false
  LinkTransform = true
  LinkedObject = -> Link013 [1.$shim-br.]
  _LinkVersion = 1
  _Parent = -> Elements001
FEATURE [Part::FeaturePython] Element038  label="shim-R-L@HGH20CA-L-Assembly"  # link proxy (typed FeaturePython)
  Detach = false
  LinkTransform = true
  LinkedObject = -> Link014 [1.$shim-tr.]
  _LinkVersion = 1
  _Parent = -> Elements001
FEATURE [Part::FeaturePython] Element040  label="shim-R-R@HGH20CA-R-Assembly"  # link proxy (typed FeaturePython)
  Detach = false
  LinkTransform = true
  LinkedObject = -> Link015 [1.$shim-br.]
  _LinkVersion = 1
  _Parent = -> Elements001
FEATURE [Part::FeaturePython] Element046  label="shim-R-L@Right plate Assembly"  # link proxy (typed FeaturePython)
  Detach = false
  LinkTransform = true
  LinkedObject = -> Link005 [1.$cart-L.]
  _LinkVersion = 1
  _Parent = -> Elements001
FEATURE [Part::FeaturePython] Element047  label="shim-R-R@Right plate Assembly"  # link proxy (typed FeaturePython)
  Detach = false
  LinkTransform = true
  LinkedObject = -> Link005 [1.$cart-R.]
  _LinkVersion = 1
  _Parent = -> Elements001
FEATURE [Part::FeaturePython] Element048  label="shim-L-L@Left plate Assembly"  # link proxy (typed FeaturePython)
  Detach = false
  LinkTransform = true
  LinkedObject = -> Link004 [1.$cart-L.]
  _LinkVersion = 1
  _Parent = -> Elements001
FEATURE [Part::FeaturePython] Element049  label="shim-L-R@Left plate Assembly"  # link proxy (typed FeaturePython)
  Detach = false
  LinkTransform = true
  LinkedObject = -> Link004 [1.$cart-R.]
  _LinkVersion = 1
  _Parent = -> Elements001
FEATURE [App::FeaturePython] Constraint021  label="Attachment-cart-R-R"  # WARN: FeaturePython — macro-defined, semantics opaque (R4)
  Cascade = false
  Disabled = false
  Group = -> [ElementLink039,ElementLink040]
  Multiply = false
  _ConstraintType = 45
  _LinkVersion = 1
  _Parent = -> Constraints001
FEATURE [App::FeaturePython] ElementLink039  label="shim-R-R@Right plate Assembly"  # link proxy (typed FeaturePython)
  LinkTransform = true
  LinkedObject = -> Element047
  Offset = pos=(0,0,0) rot=(1,0,0;3.14159rad)
  Placement = pos=(364.6,609.6,2.274e-13) rot=(0,0,1;3.14159rad)
  _LinkVersion = 1
  _Parent = -> Constraint021
FEATURE [App::FeaturePython] ElementLink040  label="shim-R-R@HGH20CA-R-Assembly"  # link proxy (typed FeaturePython)
  LinkTransform = true
  LinkedObject = -> Element040
  Offset = pos=(0,0,0) rot=(0,0,1;1.5708rad)
  Placement = pos=(-38.3,1.705e-13,402.9) rot=(0,1,0;1.5708rad)
  _LinkVersion = 1
  _Parent = -> Constraint021
FEATURE [App::FeaturePython] Constraint022  label="Attachment-cart-R-L"  # WARN: FeaturePython — macro-defined, semantics opaque (R4)
  Cascade = false
  Disabled = false
  Group = -> [ElementLink041,ElementLink042]
  Multiply = false
  _ConstraintType = 45
  _LinkVersion = 1
  _Parent = -> Constraints001
FEATURE [App::FeaturePython] ElementLink041  label="shim-R-L@Right plate Assembly"  # link proxy (typed FeaturePython)
  LinkTransform = true
  LinkedObject = -> Element046
  Offset = pos=(0,0,0) rot=(1,0,0;3.14159rad)
  Placement = pos=(364.6,609.6,2.274e-13) rot=(0,0,1;3.14159rad)
  _LinkVersion = 1
  _Parent = -> Constraint022
FEATURE [App::FeaturePython] ElementLink042  label="shim-R-L@HGH20CA-L-Assembly"  # link proxy (typed FeaturePython)
  LinkTransform = true
  LinkedObject = -> Element038
  Offset = pos=(0,0,0) rot=(0,0,1;1.5708rad)
  Placement = pos=(141.7,5.68e-14,222.9) rot=(0,1,0;1.5708rad)
  _LinkVersion = 1
  _Parent = -> Constraint022
FEATURE [App::FeaturePython] Constraint023  label="Attachment-cart-L-R"  # WARN: FeaturePython — macro-defined, semantics opaque (R4)
  Cascade = false
  Disabled = false
  Group = -> [ElementLink043,ElementLink044]
  Multiply = false
  _ConstraintType = 45
  _LinkVersion = 1
  _Parent = -> Constraints001
FEATURE [App::FeaturePython] ElementLink043  label="shim-L-R@Left plate Assembly"  # link proxy (typed FeaturePython)
  LinkTransform = true
  LinkedObject = -> Element049
  Placement = pos=(1.137e-13,0,-7.1e-15) rot=(0,0,1;0rad)
  _LinkVersion = 1
  _Parent = -> Constraint023
FEATURE [App::FeaturePython] ElementLink044  label="shim-L-R@HGH20CA-R-Assembly"  # link proxy (typed FeaturePython)
  LinkTransform = true
  LinkedObject = -> Element036
  Offset = pos=(0,0,0) rot=(0,0,1;4.71239rad)
  Placement = pos=(141.7,5.68e-14,222.9) rot=(0,1,0;1.5708rad)
  _LinkVersion = 1
  _Parent = -> Constraint023
FEATURE [App::FeaturePython] Constraint024  label="Attachment-cart-L-L"  # WARN: FeaturePython — macro-defined, semantics opaque (R4)
  Cascade = false
  Disabled = false
  Group = -> [ElementLink045,ElementLink046]
  Multiply = false
  _ConstraintType = 45
  _LinkVersion = 1
  _Parent = -> Constraints001
FEATURE [App::FeaturePython] ElementLink045  label="shim-L-L@HGH20CA-L-Assembly"  # link proxy (typed FeaturePython)
  LinkTransform = true
  LinkedObject = -> Element034
  Offset = pos=(0,0,0) rot=(0,0,1;3.14159rad)
  Placement = pos=(364.6,-4.547e-13,441.2) rot=(0,1,0;3.14159rad)
  _LinkVersion = 1
  _Parent = -> Constraint024
FEATURE [App::FeaturePython] ElementLink046  label="shim-L-L@Left plate Assembly"  # link proxy (typed FeaturePython)
  LinkTransform = true
  LinkedObject = -> Element048
  Offset = pos=(0,0,0) rot=(0,0,1;4.71239rad)
  Placement = pos=(-38.3,-5.68e-14,402.9) rot=(0,1,0;1.5708rad)
  _LinkVersion = 1
  _Parent = -> Constraint024
FEATURE [Part::FeaturePython] Element054  label="point@HGH20CA-R-Assembly"  # link proxy (typed FeaturePython)
  Detach = false
  LinkTransform = true
  LinkedObject = -> Link015 [1.$point.]
  _LinkVersion = 1
  _Parent = -> Elements001
FEATURE [Part::FeaturePython] Element055  label="side-mate@HGH20CA-R-Assembly"  # link proxy (typed FeaturePython)
  Detach = false
  LinkTransform = true
  LinkedObject = -> Link015 [1.$side-mate.]
  _LinkVersion = 1
  _Parent = -> Elements001
FEATURE [Part::FeaturePython] Element056  label="top-mate@HGH20CA-R-Assembly"  # link proxy (typed FeaturePython)
  Detach = false
  LinkTransform = true
  LinkedObject = -> Link015 [1.$top-mate.]
  _LinkVersion = 1
  _Parent = -> Elements001
FEATURE [Part::FeaturePython] Element057  label="plate-mate@Gouverner Assembly Left"  # link proxy (typed FeaturePython)
  Detach = false
  LinkTransform = true
  LinkedObject = -> Link022 [1.$plate-mate.]
  _LinkVersion = 1
  _Parent = -> Elements001
FEATURE [Part::FeaturePython] Element058  label="nut-mate@Gouverner Assembly Left"  # link proxy (typed FeaturePython)
  Detach = false
  LinkTransform = true
  LinkedObject = -> Link022 [1.$nut-mate.]
  _LinkVersion = 1
  _Parent = -> Elements001
FEATURE [Part::FeaturePython] Element059  label="plate-mate@Gouverner Assembly Right"  # link proxy (typed FeaturePython)
  Detach = false
  LinkTransform = true
  LinkedObject = -> Link023 [1.$plate-mate.]
  _LinkVersion = 1
  _Parent = -> Elements001
FEATURE [Part::FeaturePython] Element060  label="nut-mate@Gouverner Assembly Right"  # link proxy (typed FeaturePython)
  Detach = false
  LinkTransform = true
  LinkedObject = -> Link023 [1.$nut-mate.]
  _LinkVersion = 1
  _Parent = -> Elements001
FEATURE [Part::FeaturePython] Element061  label="gov-mate@Left plate Assembly"  # link proxy (typed FeaturePython)
  Detach = false
  LinkTransform = true
  LinkedObject = -> Link004 [1.$gov-mate.]
  _LinkVersion = 1
  _Parent = -> Elements001
FEATURE [Part::FeaturePython] Element062  label="gov-mate@Right plate Assembly"  # link proxy (typed FeaturePython)
  Detach = false
  LinkTransform = true
  LinkedObject = -> Link005 [1.$gov-mate.]
  _LinkVersion = 1
  _Parent = -> Elements001
FEATURE [App::FeaturePython] Constraint025  label="Attachment-governer-left"  # WARN: FeaturePython — macro-defined, semantics opaque (R4)
  Cascade = false
  Disabled = false
  Group = -> [ElementLink047,ElementLink048]
  Multiply = false
  _ConstraintType = 45
  _LinkVersion = 1
  _Parent = -> Constraints001
FEATURE [App::FeaturePython] ElementLink047  label="gov-mate@Left plate Assembly"  # link proxy (typed FeaturePython)
  LinkTransform = true
  LinkedObject = -> Element061
  _LinkVersion = 1
  _Parent = -> Constraint025
FEATURE [App::FeaturePython] ElementLink048  label="plate-mate@Gouverner Assembly Left"  # link proxy (typed FeaturePython)
  LinkTransform = true
  LinkedObject = -> Element057
  _LinkVersion = 1
  _Parent = -> Constraint025
FEATURE [App::FeaturePython] Constraint026  label="Attachment-governer-right"  # WARN: FeaturePython — macro-defined, semantics opaque (R4)
  Cascade = false
  Disabled = false
  Group = -> [ElementLink049,ElementLink050]
  Multiply = false
  _ConstraintType = 45
  _LinkVersion = 1
  _Parent = -> Constraints001
FEATURE [App::FeaturePython] ElementLink049  label="gov-mate@Right plate Assembly"  # link proxy (typed FeaturePython)
  LinkTransform = true
  LinkedObject = -> Element062
  _LinkVersion = 1
  _Parent = -> Constraint026
FEATURE [App::FeaturePython] ElementLink050  label="plate-mate@Gouverner Assembly Right"  # link proxy (typed FeaturePython)
  LinkTransform = true
  LinkedObject = -> Element059
  _LinkVersion = 1
  _Parent = -> Constraint026
FEATURE [Part::FeaturePython] Element063  label="gov-mate@NUT Assembly"  # link proxy (typed FeaturePython)
  Detach = false
  LinkTransform = true
  LinkedObject = -> Link020 [1.$gov-mate.]
  _LinkVersion = 1
  _Parent = -> Elements001
FEATURE [App::FeaturePython] Constraint027  label="Attachment-nut-governer-left"  # WARN: FeaturePython — macro-defined, semantics opaque (R4)
  Cascade = false
  Disabled = false
  Group = -> [ElementLink051,ElementLink052]
  Multiply = false
  _ConstraintType = 45
  _LinkVersion = 1
  _Parent = -> Constraints001
FEATURE [App::FeaturePython] ElementLink051  label="gov-mate@NUT Assembly"  # link proxy (typed FeaturePython)
  LinkTransform = true
  LinkedObject = -> Element063
  _LinkVersion = 1
  _Parent = -> Constraint027
FEATURE [App::FeaturePython] ElementLink052  label="nut-mate@Gouverner Assembly Left"  # link proxy (typed FeaturePython)
  LinkTransform = true
  LinkedObject = -> Element058
  Offset = pos=(0,0,0) rot=(0,0,1;1.5708rad)
  Placement = pos=(341.9,2.274e-13,-56.7) rot=(0,-1,0;1.5708rad)
  _LinkVersion = 1
  _Parent = -> Constraint027
FEATURE [Part::FeaturePython] Element064  label="gov-mate-r@NUT Assembly"  # link proxy (typed FeaturePython)
  Detach = false
  LinkTransform = true
  LinkedObject = -> Link021 [1.$gov-mate-r.]
  _LinkVersion = 1
  _Parent = -> Elements001
FEATURE [App::FeaturePython] Constraint028  label="Attachment-nut-governer-right"  # WARN: FeaturePython — macro-defined, semantics opaque (R4)
  Cascade = false
  Disabled = false
  Group = -> [ElementLink053,ElementLink054]
  Multiply = false
  _ConstraintType = 45
  _LinkVersion = 1
  _Parent = -> Constraints001
FEATURE [App::FeaturePython] ElementLink053  label="gov-mate-r@NUT Assembly"  # link proxy (typed FeaturePython)
  LinkTransform = true
  LinkedObject = -> Element064
  _LinkVersion = 1
  _Parent = -> Constraint028
FEATURE [App::FeaturePython] ElementLink054  label="nut-mate@Gouverner Assembly Right"  # link proxy (typed FeaturePython)
  LinkTransform = true
  LinkedObject = -> Element060
  Offset = pos=(0,0,0) rot=(0,0,1;4.71239rad)
  Placement = pos=(317.9,-5.68e-14,-80.7) rot=(0,-1,0;1.5708rad)
  _LinkVersion = 1
  _Parent = -> Constraint028
FEATURE [App::FeaturePython] Constraint029  label="Attachment-stepper-plate"  # WARN: FeaturePython — macro-defined, semantics opaque (R4)
  Cascade = false
  Disabled = false
  Group = -> [ElementLink055,ElementLink056]
  Multiply = false
  _ConstraintType = 45
  _LinkVersion = 1
  _Parent = -> Constraints001
FEATURE [App::FeaturePython] ElementLink055  label="plate-mate@NEMA23-76-Assembly"  # link proxy (typed FeaturePython)
  LinkTransform = true
  LinkedObject = -> Element025
  _LinkVersion = 1
  _Parent = -> Constraint029
FEATURE [App::FeaturePython] ElementLink056  label="motor-mate@Left plate Assembly"  # link proxy (typed FeaturePython)
  LinkTransform = true
  LinkedObject = -> Element026
  Offset = pos=(0,0,0) rot=(1,0,0;3.14159rad)
  Placement = pos=(-55.7,-647.7,-1.705e-13) rot=(0,0,1;3.14159rad)
  _LinkVersion = 1
  _Parent = -> Constraint029
FEATURE [App::DocumentObjectGroup] Group  label="Components"
  ExportMode = 1
  Group = -> [Assembly,Assembly002]
  _GroupVersion = 1
FEATURE [Part::FeaturePython] Assembly002  label="1/4x1/2 screw and washer Assembly"  # WARN: FeaturePython — macro-defined, semantics opaque (R4)
  AutoRelax = true
  BuildShape = 0
  Freeze = false
  Group = -> [Constraints002,Elements002,Parts002]
  Verbose = false
  _LinkVersion = 1
  _SolverType = 1
  _Version = 1
FEATURE [App::FeaturePython] Constraints002  # WARN: FeaturePython — macro-defined, semantics opaque (R4)
  Group = -> [Constraint030,Constraint031]
  _LinkVersion = 1
  _Version = 1
FEATURE [App::FeaturePython] Elements002  # WARN: FeaturePython — macro-defined, semantics opaque (R4)
  Group = -> [_Element,_Element001,Element065]
  _LinkVersion = 1
FEATURE [App::FeaturePython] Constraint030  label="Locked002"  # WARN: FeaturePython — macro-defined, semantics opaque (R4)
  Disabled = false
  Group = -> [ElementLink057]
  _ConstraintType = 0
  _LinkVersion = 1
  _Parent = -> Constraints002
FEATURE [App::FeaturePython] ElementLink057  label="_Element"  # link proxy (typed FeaturePython)
  LinkTransform = true
  LinkedObject = -> _Element
  _LinkVersion = 1
  _Parent = -> Constraint030
FEATURE [Part::FeaturePython] _Element  # link proxy (typed FeaturePython)
  Detach = false
  LinkTransform = true
  LinkedObject = -> Screw [Edge4]
  _LinkVersion = 1
  _Parent = -> Elements002
FEATURE [App::FeaturePython] Constraint031  label="Attachment001"  # WARN: FeaturePython — macro-defined, semantics opaque (R4)
  Cascade = false
  Disabled = false
  Group = -> [ElementLink058,ElementLink059]
  Multiply = false
  _ConstraintType = 45
  _LinkVersion = 1
  _Parent = -> Constraints002
FEATURE [App::FeaturePython] ElementLink058  label="_Element001"  # link proxy (typed FeaturePython)
  LinkTransform = true
  LinkedObject = -> _Element001
  _LinkVersion = 1
  _Parent = -> Constraint031
FEATURE [Part::FeaturePython] _Element001  # link proxy (typed FeaturePython)
  Detach = false
  LinkTransform = true
  LinkedObject = -> Washer [Edge1]
  _LinkVersion = 1
  _Parent = -> Elements002
FEATURE [App::FeaturePython] ElementLink059  label="_Element"  # link proxy (typed FeaturePython)
  LinkTransform = true
  LinkedObject = -> _Element
  _LinkVersion = 1
  _Parent = -> Constraint031
FEATURE [Part::FeaturePython] Element065  label="mate"  # link proxy (typed FeaturePython)
  Detach = false
  LinkTransform = true
  LinkedObject = -> Washer [Edge5]
  _LinkVersion = 1
  _Parent = -> Elements002
FEATURE [App::FeaturePython] Constraint032  label="Attachment002"  # WARN: FeaturePython — macro-defined, semantics opaque (R4)
  Cascade = false
  Disabled = false
  Group = -> [ElementLink060,ElementLink061]
  Multiply = false
  _ConstraintType = 45
  _LinkVersion = 1
  _Parent = -> Constraints
FEATURE [App::FeaturePython] ElementLink060  label="_Element002"  # link proxy (typed FeaturePython)
  LinkTransform = true
  LinkedObject = -> _Element002
  Offset = pos=(0,0,0) rot=(1,0,0;3.14159rad)
  Placement = pos=(-123.62,0,-25.4) rot=(0,1,0;3.14159rad)
  _LinkVersion = 1
  _Parent = -> Constraint032
FEATURE [Part::FeaturePython] _Element002  # link proxy (typed FeaturePython)
  Detach = false
  LinkTransform = true
  LinkedObject = -> Link025 [Link025_i0.1.$mate.]
  _LinkVersion = 1
  _Parent = -> Elements
FEATURE [App::FeaturePython] ElementLink061  label="_Element003"  # link proxy (typed FeaturePython)
  LinkTransform = true
  LinkedObject = -> _Element003
  _LinkVersion = 1
  _Parent = -> Constraint032
FEATURE [Part::FeaturePython] _Element003  # link proxy (typed FeaturePython)
  Detach = false
  LinkTransform = true
  LinkedObject = -> Link024 [Sketch007.Edge2]
  _LinkVersion = 1
  _Parent = -> Elements
FEATURE [App::FeaturePython] Constraint033  label="Attachment003"  # WARN: FeaturePython — macro-defined, semantics opaque (R4)
  Cascade = false
  Disabled = false
  Group = -> [ElementLink062,ElementLink063]
  Multiply = false
  _ConstraintType = 45
  _LinkVersion = 1
  _Parent = -> Constraints
FEATURE [App::FeaturePython] ElementLink062  label="_Element004"  # link proxy (typed FeaturePython)
  LinkTransform = true
  LinkedObject = -> _Element004
  Offset = pos=(0,0,0) rot=(1,0,0;3.14159rad)
  Placement = pos=(-123.62,0,-25.4) rot=(0,1,0;3.14159rad)
  _LinkVersion = 1
  _Parent = -> Constraint033
FEATURE [Part::FeaturePython] _Element004  # link proxy (typed FeaturePython)
  Detach = false
  LinkTransform = true
  LinkedObject = -> Link025 [Link025_i1.1.$mate.]
  _LinkVersion = 1
  _Parent = -> Elements
FEATURE [App::FeaturePython] ElementLink063  label="_Element005"  # link proxy (typed FeaturePython)
  LinkTransform = true
  LinkedObject = -> _Element005
  _LinkVersion = 1
  _Parent = -> Constraint033
FEATURE [Part::FeaturePython] _Element005  # link proxy (typed FeaturePython)
  Detach = false
  LinkTransform = true
  LinkedObject = -> Link024 [Sketch007.Edge6]
  _LinkVersion = 1
  _Parent = -> Elements
FEATURE [App::FeaturePython] Constraint034  label="Attachment004"  # WARN: FeaturePython — macro-defined, semantics opaque (R4)
  Cascade = false
  Disabled = false
  Group = -> [ElementLink064,ElementLink065]
  Multiply = false
  _ConstraintType = 45
  _LinkVersion = 1
  _Parent = -> Constraints
FEATURE [App::FeaturePython] ElementLink064  label="_Element006"  # link proxy (typed FeaturePython)
  LinkTransform = true
  LinkedObject = -> _Element006
  Offset = pos=(0,0,0) rot=(1,0,0;3.14159rad)
  Placement = pos=(-123.62,0,-25.4) rot=(0,1,0;3.14159rad)
  _LinkVersion = 1
  _Parent = -> Constraint034
FEATURE [Part::FeaturePython] _Element006  # link proxy (typed FeaturePython)
  Detach = false
  LinkTransform = true
  LinkedObject = -> Link025 [Link025_i2.1.$mate.]
  _LinkVersion = 1
  _Parent = -> Elements
FEATURE [App::FeaturePython] ElementLink065  label="_Element007"  # link proxy (typed FeaturePython)
  LinkTransform = true
  LinkedObject = -> _Element007
  _LinkVersion = 1
  _Parent = -> Constraint034
FEATURE [Part::FeaturePython] _Element007  # link proxy (typed FeaturePython)
  Detach = false
  LinkTransform = true
  LinkedObject = -> Link024 [Sketch007.Edge4]
  _LinkVersion = 1
  _Parent = -> Elements
FEATURE [App::FeaturePython] Constraint035  label="Attachment005"  # WARN: FeaturePython — macro-defined, semantics opaque (R4)
  Cascade = false
  Disabled = false
  Group = -> [ElementLink066,ElementLink067]
  Multiply = false
  _ConstraintType = 45
  _LinkVersion = 1
  _Parent = -> Constraints
FEATURE [App::FeaturePython] ElementLink066  label="_Element008"  # link proxy (typed FeaturePython)
  LinkTransform = true
  LinkedObject = -> _Element008
  Offset = pos=(0,0,0) rot=(1,0,0;3.14159rad)
  Placement = pos=(-123.62,0,-25.4) rot=(0,1,0;3.14159rad)
  _LinkVersion = 1
  _Parent = -> Constraint035
FEATURE [Part::FeaturePython] _Element008  # link proxy (typed FeaturePython)
  Detach = false
  LinkTransform = true
  LinkedObject = -> Link025 [Link025_i3.1.$mate.]
  _LinkVersion = 1
  _Parent = -> Elements
FEATURE [App::FeaturePython] ElementLink067  label="_Element009"  # link proxy (typed FeaturePython)
  LinkTransform = true
  LinkedObject = -> _Element009
  _LinkVersion = 1
  _Parent = -> Constraint035
FEATURE [Part::FeaturePython] _Element009  # link proxy (typed FeaturePython)
  Detach = false
  LinkTransform = true
  LinkedObject = -> Link024 [Sketch007.Edge1]
  _LinkVersion = 1
  _Parent = -> Elements
FEATURE [Part::FeaturePython] Element066  label="limit-mate@Left plate Assembly"  # link proxy (typed FeaturePython)
  Detach = false
  LinkTransform = true
  LinkedObject = -> Link004 [1.$limit-mate.]
  _LinkVersion = 1
  _Parent = -> Elements001
FEATURE [Part::FeaturePython] Element067  label="mate l@Limit sensor Assembly"  # link proxy (typed FeaturePython)
  Detach = false
  LinkTransform = true
  LinkedObject = -> Link026 [1.$mate l.]
  _LinkVersion = 1
  _Parent = -> Elements001
FEATURE [App::FeaturePython] Constraint036  label="Attachment-limit-sensor"  # WARN: FeaturePython — macro-defined, semantics opaque (R4)
  Cascade = false
  Disabled = false
  Group = -> [ElementLink068,ElementLink069]
  Multiply = false
  _ConstraintType = 45
  _LinkVersion = 1
  _Parent = -> Constraints001
FEATURE [App::FeaturePython] ElementLink068  label="mate l@Limit sensor Assembly"  # link proxy (typed FeaturePython)
  LinkTransform = true
  LinkedObject = -> Element067
  Offset = pos=(0,0,0) rot=(0,0,1;1.5708rad)
  Placement = pos=(-22.8,0,114) rot=(0,-1,0;1.5708rad)
  _LinkVersion = 1
  _Parent = -> Constraint036
FEATURE [App::FeaturePython] ElementLink069  label="limit-mate@Left plate Assembly"  # link proxy (typed FeaturePython)
  LinkTransform = true
  LinkedObject = -> Element066
  Offset = pos=(0,0,0) rot=(1,0,0;3.14159rad)
  Placement = pos=(-136.8,-609.6,-1.563e-13) rot=(0,0,1;3.14159rad)
  _LinkVersion = 1
  _Parent = -> Constraint036
FEATURE [Part::FeaturePython] _Element010  label="_top-beam-mate@Right plate Assembly"  # link proxy (typed FeaturePython)
  Detach = false
  LinkTransform = true
  LinkedObject = -> Link005 [1.$Element044.]
  _LinkVersion = 0
  _Parent = -> Elements001
---- part Y-axis.FCStd = doc fcstd_5ea0ce396be3 (103666 chars; too large to inline — full recipe in that document) ----
---- part Z-axis.FCStd = doc fcstd_c11bbb07173d ----
FCSTD DOCUMENT  (FreeCAD 2021.717R24301 +3842 (Git))
Label: Z-axis
License: Creative Commons Attribution
LicenseURL: http://creativecommons.org/licenses/by/4.0/
objects: App::FeaturePython×43, Part::FeaturePython×38, App::Link×14
note: 37 computed .brp shape members not serialized (recipe doc carries the construction recipe); baked Part::Feature solids carry a one-line shape summary decoded from their .brp
EXTERNAL_REF file=parts/Ballscrew.FCStd obj=Assembly002
EXTERNAL_REF file=parts/Z axis plates.FCStd obj=Assembly
EXTERNAL_REF file=parts/HGR20.FCStd obj=Assembly
EXTERNAL_REF file=parts/Z axis plates.FCStd obj=Assembly004
EXTERNAL_REF file=parts/NEMA23-76.FCStd obj=Assembly
EXTERNAL_REF file=parts/NEMA23-76.FCStd obj=Assembly001
EXTERNAL_REF file=parts/BallNut.FCStd obj=Assembly
EXTERNAL_REF file=parts/Z axis plates.FCStd obj=Assembly005
EXTERNAL_REF file=parts/HGH20CA.FCStd obj=Assembly
EXTERNAL_REF file=parts/HGH20CA.FCStd obj=Assembly001
EXTERNAL_REF file=parts/LimitSensor.FCStd obj=Assembly

FEATURE [App::Link] Link007  label="Ballscrew"
  AutoLinkLabel = true
  AutoPlacement = true
  LinkPlacement = pos=(0.026908,-40.4231,-69.025) rot=(-1,0,0;4.71239rad)
  LinkedObject = -> <external parts/Ballscrew.FCStd>#Assembly002
  Placement = pos=(0.026908,-40.4231,-69.025) rot=(-1,0,0;4.71239rad)
  SyncGroupVisibility = false
  _LinkVersion = 1
FEATURE [App::Link] Link  label="Backplate"
  AutoLinkLabel = true
  AutoPlacement = true
  LinkedObject = -> <external parts/Z axis plates.FCStd>#Assembly
  SyncGroupVisibility = false
  _LinkVersion = 1
FEATURE [App::Link] Link011  label="HGR20-300-R"
  AutoLinkLabel = true
  AutoPlacement = true
  LinkPlacement = pos=(54,-15.7,-6.00267e-11) rot=(1,0,0;1.5708rad)
  LinkedObject = -> <external parts/HGR20.FCStd>#Assembly
  Placement = pos=(54,-15.7,-6.00267e-11) rot=(1,0,0;1.5708rad)
  SyncGroupVisibility = false
  _LinkVersion = 1
FEATURE [App::Link] Link012  label="HGR20-300-L"
  AutoLinkLabel = true
  AutoPlacement = true
  LinkPlacement = pos=(-54,-15.7,-5.99982e-11) rot=(1,0,0;1.5708rad)
  LinkedObject = -> <external parts/HGR20.FCStd>#Assembly
  Placement = pos=(-54,-15.7,-5.99982e-11) rot=(1,0,0;1.5708rad)
  SyncGroupVisibility = false
  _LinkVersion = 1
FEATURE [App::Link] Link017  label="Motor Bracket"
  AutoLinkLabel = true
  AutoPlacement = true
  LinkedObject = -> <external parts/Z axis plates.FCStd>#Assembly004
  SyncGroupVisibility = false
  _LinkVersion = 1
FEATURE [App::Link] Link018  label="NEMA23-76"
  AutoLinkLabel = true
  AutoPlacement = true
  LinkPlacement = pos=(0,-40.7,158.85) rot=(0,0,1;3.14159rad)
  LinkedObject = -> <external parts/NEMA23-76.FCStd>#Assembly
  Placement = pos=(0,-40.7,158.85) rot=(0,0,1;3.14159rad)
  SyncGroupVisibility = false
  _LinkVersion = 1
FEATURE [App::Link] Link019  label="Coupling"
  AutoLinkLabel = true
  AutoPlacement = true
  LinkPlacement = pos=(3e-16,-40.7,131.25) rot=(0,1,0;3.14159rad)
  LinkedObject = -> <external parts/NEMA23-76.FCStd>#Assembly001
  Placement = pos=(3e-16,-40.7,131.25) rot=(0,1,0;3.14159rad)
  SyncGroupVisibility = false
  _LinkVersion = 1
FEATURE [App::Link] Link026  label="X-Nut"
  AutoLinkLabel = true
  AutoPlacement = true
  LinkPlacement = pos=(9.875,36.75,-60.65) rot=(-0.57735,-0.57735,-0.57735;2.0944rad)
  LinkedObject = -> <external parts/BallNut.FCStd>#Assembly
  Placement = pos=(9.875,36.75,-60.65) rot=(-0.57735,-0.57735,-0.57735;2.0944rad)
  SyncGroupVisibility = false
  _LinkVersion = 1
FEATURE [App::Link] Link027  label="Nut-shim-X"
  AutoLinkLabel = true
  AutoPlacement = true
  LinkPlacement = pos=(35.475,-6.6e-15,68.35) rot=(0,1,0;4.71239rad)
  LinkedObject = -> <external parts/Z axis plates.FCStd>#Assembly005
  Placement = pos=(35.475,-6.6e-15,68.35) rot=(0,1,0;4.71239rad)
  SyncGroupVisibility = false
  _LinkVersion = 1
FEATURE [App::Link] Link028  label="HGH20CA-L-B"
  AutoLinkLabel = true
  AutoPlacement = true
  LinkPlacement = pos=(-51.25,30,-130.5) rot=(0.57735,0.57735,-0.57735;2.0944rad)
  LinkedObject = -> <external parts/HGH20CA.FCStd>#Assembly
  Placement = pos=(-51.25,30,-130.5) rot=(0.57735,0.57735,-0.57735;2.0944rad)
  SyncGroupVisibility = false
  _LinkVersion = 1
FEATURE [App::Link] Link029  label="HGH20CA-R-B"
  AutoLinkLabel = true
  AutoPlacement = true
  LinkPlacement = pos=(51.25,30,-130.5) rot=(0.57735,0.57735,-0.57735;2.0944rad)
  LinkedObject = -> <external parts/HGH20CA.FCStd>#Assembly001
  Placement = pos=(51.25,30,-130.5) rot=(0.57735,0.57735,-0.57735;2.0944rad)
  SyncGroupVisibility = false
  _LinkVersion = 1
FEATURE [App::Link] Link030  label="HGH20CA-R-T"
  AutoLinkLabel = true
  AutoPlacement = true
  LinkPlacement = pos=(51.25,30,9.2) rot=(0.57735,-0.57735,0.57735;2.0944rad)
  LinkedObject = -> <external parts/HGH20CA.FCStd>#Assembly
  Placement = pos=(51.25,30,9.2) rot=(0.57735,-0.57735,0.57735;2.0944rad)
  SyncGroupVisibility = false
  _LinkVersion = 1
FEATURE [App::Link] Link031  label="HGH20CA-L-T"
  AutoLinkLabel = true
  AutoPlacement = true
  LinkPlacement = pos=(-51.25,30,9.2) rot=(0.57735,-0.57735,0.57735;2.0944rad)
  LinkedObject = -> <external parts/HGH20CA.FCStd>#Assembly001
  Placement = pos=(-51.25,30,9.2) rot=(0.57735,-0.57735,0.57735;2.0944rad)
  SyncGroupVisibility = false
  _LinkVersion = 1
FEATURE [App::Link] Link032  label="Limit sensor"
  AutoLinkLabel = true
  AutoPlacement = true
  LinkPlacement = pos=(-54,-61.85,152.5) rot=(0,0.707107,0.707107;3.14159rad)
  LinkedObject = -> <external parts/LimitSensor.FCStd>#Assembly
  Placement = pos=(-54,-61.85,152.5) rot=(0,0.707107,0.707107;3.14159rad)
  SyncGroupVisibility = false
  _LinkVersion = 1
FEATURE [Part::FeaturePython] Parts  # WARN: FeaturePython — macro-defined, semantics opaque (R4)
  Group = -> [Link007,Link,Link011,Link012,Link017,Link018,Link019,Link026,Link027,Link028,Link029,Link030,Link031,Link032]
  GroupMode = 0
  _LinkVersion = 1
FEATURE [Part::FeaturePython] Assembly  label="Z-axis assembly"  # WARN: FeaturePython — macro-defined, semantics opaque (R4)
  AutoRelax = true
  BuildShape = 0
  Freeze = false
  Group = -> [Constraints,Elements,Parts]
  Verbose = false
  _LinkVersion = 1
  _SolverType = 1
  _Version = 1
FEATURE [App::FeaturePython] Elements  # WARN: FeaturePython — macro-defined, semantics opaque (R4)
  Group = -> [Element,Element001,Element002,Element004,Element005,Element006,Element007,Element009,Element011,Element033,Element034,Element035,Element036,Element037,Element039,Element040,Element041,Element042,Element043,Element044,Element053,Element054,Element055,Element056,Element057,Element058,Element059,Element060,Element061,Element062,Element063,Element064,_Element,_Element001,Element065,_Element002]
  _LinkVersion = 1
FEATURE [Part::FeaturePython] Element  label="rail-tr@Backplate-Assembly"  # link proxy (typed FeaturePython)
  Detach = false
  LinkTransform = true
  LinkedObject = -> Link [1.$rail-tr.]
  _LinkVersion = 1
  _Parent = -> Elements
FEATURE [Part::FeaturePython] Element001  label="rail-bl@Backplate-Assembly"  # link proxy (typed FeaturePython)
  Detach = false
  LinkTransform = true
  LinkedObject = -> Link [1.$rail-tl.]
  _LinkVersion = 1
  _Parent = -> Elements
FEATURE [Part::FeaturePython] Element002  label="screw-br@Backplate-Assembly"  # link proxy (typed FeaturePython)
  Detach = false
  LinkTransform = true
  LinkedObject = -> Link [1.$screw-br.]
  _LinkVersion = 1
  _Parent = -> Elements
FEATURE [Part::FeaturePython] Element004  label="BP-mate@Ballscrew-Assembly"  # link proxy (typed FeaturePython)
  Detach = false
  LinkTransform = true
  LinkedObject = -> Link007 [1.$BP-mate.]
  _LinkVersion = 1
  _Parent = -> Elements
FEATURE [Part::FeaturePython] Element005  label="BP-mate-r@HGR20-300-Assembly"  # link proxy (typed FeaturePython)
  Detach = false
  LinkTransform = true
  LinkedObject = -> Link011 [1.$BP-mate-r.]
  _LinkVersion = 1
  _Parent = -> Elements
FEATURE [Part::FeaturePython] Element006  label="r-mate@HGR20-300-Assembly"  # link proxy (typed FeaturePython)
  Detach = false
  LinkTransform = true
  LinkedObject = -> Link011 [1.$r-mate.]
  _LinkVersion = 1
  _Parent = -> Elements
FEATURE [Part::FeaturePython] Element007  label="top-mate@HGR20-300-Assembly"  # link proxy (typed FeaturePython)
  Detach = false
  LinkTransform = true
  LinkedObject = -> Link011 [1.$top-mate.]
  _LinkVersion = 1
  _Parent = -> Elements
FEATURE [Part::FeaturePython] Element009  label="BP-mate-r@HGR20-300-Assembly001"  # link proxy (typed FeaturePython)
  Detach = false
  LinkTransform = true
  LinkedObject = -> Link012 [1.$BP-mate-r.]
  _LinkVersion = 1
  _Parent = -> Elements
FEATURE [Part::FeaturePython] Element011  label="Axis@Ballscrew-Assembly"  # link proxy (typed FeaturePython)
  Detach = false
  LinkTransform = true
  LinkedObject = -> Link007 [1.$Axis.]
  _LinkVersion = 1
  _Parent = -> Elements
FEATURE [Part::FeaturePython] Element033  label="point@HGR20-300-Assembly"  # link proxy (typed FeaturePython)
  Detach = false
  LinkTransform = true
  LinkedObject = -> Link011 [1.$point.]
  _LinkVersion = 1
  _Parent = -> Elements
FEATURE [App::FeaturePython] ElementLink  label="rail-tr@Backplate-Assembly"  # link proxy (typed FeaturePython)
  LinkTransform = true
  LinkedObject = -> Element
  _LinkVersion = 1
  _Parent = -> Constraint
FEATURE [App::FeaturePython] Constraint  label="Locked"  # WARN: FeaturePython — macro-defined, semantics opaque (R4)
  Disabled = false
  Group = -> [ElementLink]
  _ConstraintType = 0
  _LinkVersion = 1
  _Parent = -> Constraints
FEATURE [App::FeaturePython] ElementLink002  label="screw-br@Backplate-Assembly"  # link proxy (typed FeaturePython)
  LinkTransform = true
  LinkedObject = -> Element002
  Offset = pos=(0,0,0) rot=(0,0,1;3.14159rad)
  Placement = pos=(46,5.33e-14,-241.05) rot=(0,1,0;3.14159rad)
  _LinkVersion = 1
  _Parent = -> Constraint001
FEATURE [App::FeaturePython] ElementLink007  label="BP-mate@Ballscrew-Assembly"  # link proxy (typed FeaturePython)
  LinkTransform = true
  LinkedObject = -> Element004
  Offset = pos=(0,0,0) rot=(1,0,0;3.14159rad)
  Placement = pos=(-2.84e-14,-31.4,-241.05) rot=(1,0,0;3.14159rad)
  _LinkVersion = 1
  _Parent = -> Constraint001
FEATURE [App::FeaturePython] Constraint001  label="Attachment-BP-Screw"  # WARN: FeaturePython — macro-defined, semantics opaque (R4)
  Cascade = false
  Disabled = false
  Group = -> [ElementLink002,ElementLink007]
  Multiply = false
  _ConstraintType = 45
  _LinkVersion = 1
  _Parent = -> Constraints
FEATURE [App::FeaturePython] ElementLink008  label="rail-tr@Backplate-Assembly"  # link proxy (typed FeaturePython)
  LinkTransform = true
  LinkedObject = -> Element
  _LinkVersion = 1
  _Parent = -> Constraint002
FEATURE [App::FeaturePython] ElementLink009  label="BP-mate-r@HGR20-300-Assembly"  # link proxy (typed FeaturePython)
  LinkTransform = true
  LinkedObject = -> Element005
  Offset = pos=(0,0,0) rot=(0,0,1;3.14159rad)
  Placement = pos=(108,5.51e-14,240) rot=(0,1,0;3.14159rad)
  _LinkVersion = 1
  _Parent = -> Constraint002
FEATURE [App::FeaturePython] Constraint002  label="Attachment-BP-rail-r"  # WARN: FeaturePython — macro-defined, semantics opaque (R4)
  Cascade = false
  Disabled = false
  Group = -> [ElementLink008,ElementLink009]
  Multiply = false
  _ConstraintType = 45
  _LinkVersion = 1
  _Parent = -> Constraints
FEATURE [App::FeaturePython] ElementLink010  label="rail-bl@Backplate-Assembly"  # link proxy (typed FeaturePython)
  LinkTransform = true
  LinkedObject = -> Element001
  _LinkVersion = 1
  _Parent = -> Constraint003
FEATURE [App::FeaturePython] ElementLink011  label="BP-mate-r@HGR20-300-Assembly001"  # link proxy (typed FeaturePython)
  LinkTransform = true
  LinkedObject = -> Element009
  _LinkVersion = 1
  _Parent = -> Constraint003
FEATURE [App::FeaturePython] Constraint003  label="Attachment-BP-rail-l"  # WARN: FeaturePython — macro-defined, semantics opaque (R4)
  Cascade = false
  Disabled = false
  Group = -> [ElementLink010,ElementLink011]
  Multiply = false
  _ConstraintType = 45
  _LinkVersion = 1
  _Parent = -> Constraints
FEATURE [App::FeaturePython] Constraints  # WARN: FeaturePython — macro-defined, semantics opaque (R4)
  Group = -> [Constraint,Constraint001,Constraint002,Constraint003,Constraint016,Constraint017,Constraint018,Constraint019,Constraint020,Constraint023,Constraint025,Constraint026,Constraint027,Constraint028]
  _LinkVersion = 1
  _Version = 1
FEATURE [Part::FeaturePython] Element034  label="bp-mate@Motor Bracket Assembly"  # link proxy (typed FeaturePython)
  Detach = false
  LinkTransform = true
  LinkedObject = -> Link017 [1.$bp-mate.]
  _LinkVersion = 1
  _Parent = -> Elements
FEATURE [Part::FeaturePython] Element035  label="Motor-mate@Motor Bracket Assembly"  # link proxy (typed FeaturePython)
  Detach = false
  LinkTransform = true
  LinkedObject = -> Link017 [1.$Motor-mate.]
  _LinkVersion = 1
  _Parent = -> Elements
FEATURE [Part::FeaturePython] Element036  label="bracket-mate@Backplate-Assembly"  # link proxy (typed FeaturePython)
  Detach = false
  LinkTransform = true
  LinkedObject = -> Link [1.$bracket-mate.]
  _LinkVersion = 1
  _Parent = -> Elements
FEATURE [App::FeaturePython] Constraint016  label="Attachment-BP-bracket"  # WARN: FeaturePython — macro-defined, semantics opaque (R4)
  Cascade = false
  Disabled = false
  Group = -> [ElementLink036,ElementLink037]
  Multiply = false
  _ConstraintType = 45
  _LinkVersion = 1
  _Parent = -> Constraints
FEATURE [App::FeaturePython] ElementLink036  label="bracket-mate@Backplate-Assembly"  # link proxy (typed FeaturePython)
  LinkTransform = true
  LinkedObject = -> Element036
  _LinkVersion = 1
  _Parent = -> Constraint016
FEATURE [App::FeaturePython] ElementLink037  label="bp-mate@Motor Bracket Assembly"  # link proxy (typed FeaturePython)
  LinkTransform = true
  LinkedObject = -> Element034
  _LinkVersion = 1
  _Parent = -> Constraint016
FEATURE [Part::FeaturePython] Element037  label="bracket-mate@NEMA23-76-Assembly"  # link proxy (typed FeaturePython)
  Detach = false
  LinkTransform = true
  LinkedObject = -> Link018 [1.$bracket-mate.]
  _LinkVersion = 1
  _Parent = -> Elements
FEATURE [App::FeaturePython] Constraint017  label="Attachment-motor"  # WARN: FeaturePython — macro-defined, semantics opaque (R4)
  Cascade = false
  Disabled = false
  Group = -> [ElementLink038,ElementLink039]
  Multiply = false
  _ConstraintType = 45
  _LinkVersion = 1
  _Parent = -> Constraints
FEATURE [App::FeaturePython] ElementLink038  label="bracket-mate@NEMA23-76-Assembly"  # link proxy (typed FeaturePython)
  LinkTransform = true
  LinkedObject = -> Element037
  Offset = pos=(0,0,0) rot=(1,0,0;3.14159rad)
  Placement = pos=(-1e-14,-81.4,317.7) rot=(1,0,0;3.14159rad)
  _LinkVersion = 1
  _Parent = -> Constraint017
FEATURE [App::FeaturePython] ElementLink039  label="Motor-mate@Motor Bracket Assembly"  # link proxy (typed FeaturePython)
  LinkTransform = true
  LinkedObject = -> Element035
  _LinkVersion = 1
  _Parent = -> Constraint017
FEATURE [Part::FeaturePython] Element039  label="coupling-mate@NEMA23-76-Assembly"  # link proxy (typed FeaturePython)
  Detach = false
  LinkTransform = true
  LinkedObject = -> Link018 [1.$coupling-mate.]
  _LinkVersion = 1
  _Parent = -> Elements
FEATURE [Part::FeaturePython] Element040  label="motor-mate@Coupling-Assembly"  # link proxy (typed FeaturePython)
  Detach = false
  LinkTransform = true
  LinkedObject = -> Link019 [1.$motor-mate.]
  _LinkVersion = 1
  _Parent = -> Elements
FEATURE [App::FeaturePython] Constraint018  label="Attachment-coupling"  # WARN: FeaturePython — macro-defined, semantics opaque (R4)
  Cascade = false
  Disabled = false
  Group = -> [ElementLink040,ElementLink041]
  Multiply = false
  _ConstraintType = 45
  _LinkVersion = 1
  _Parent = -> Constraints
FEATURE [App::FeaturePython] ElementLink040  label="coupling-mate@NEMA23-76-Assembly"  # link proxy (typed FeaturePython)
  LinkTransform = true
  LinkedObject = -> Element039
  _LinkVersion = 1
  _Parent = -> Constraint018
FEATURE [App::FeaturePython] ElementLink041  label="motor-mate@Coupling-Assembly"  # link proxy (typed FeaturePython)
  LinkTransform = true
  LinkedObject = -> Element040
  _LinkVersion = 1
  _Parent = -> Constraint018
FEATURE [Part::FeaturePython] Element041  label="X-cart-BP-br@HGH20CA-R-Assembly002"  # link proxy (typed FeaturePython)
  Detach = false
  LinkTransform = true
  LinkedObject = -> Link029 [1.$shim-br.]
  _LinkVersion = 1
  _Parent = -> Elements
FEATURE [Part::FeaturePython] Element042  label="X-cart-BP-bl@HGH20CA-L-Assembly002"  # link proxy (typed FeaturePython)
  Detach = false
  LinkTransform = true
  LinkedObject = -> Link028 [1.$shim-tr.]
  _LinkVersion = 1
  _Parent = -> Elements
FEATURE [Part::FeaturePython] Element043  label="x-cart-bl@Backplate-Assembly"  # link proxy (typed FeaturePython)
  Detach = false
  LinkTransform = true
  LinkedObject = -> Link [1.$x-cart-bl.]
  _LinkVersion = 1
  _Parent = -> Elements
FEATURE [Part::FeaturePython] Element044  label="x-cart-br@Backplate-Assembly"  # link proxy (typed FeaturePython)
  Detach = false
  LinkTransform = true
  LinkedObject = -> Link [1.$x-cart-br.]
  _LinkVersion = 1
  _Parent = -> Elements
FEATURE [App::FeaturePython] Constraint019  label="Attachment-x-cart-br"  # WARN: FeaturePython — macro-defined, semantics opaque (R4)
  Cascade = false
  Disabled = false
  Group = -> [ElementLink042,ElementLink043]
  Multiply = false
  _ConstraintType = 45
  _LinkVersion = 1
  _Parent = -> Constraints
FEATURE [App::FeaturePython] ElementLink042  label="x-cart-br@Backplate-Assembly"  # link proxy (typed FeaturePython)
  LinkTransform = true
  LinkedObject = -> Element044
  Offset = pos=(0,0,0) rot=(1,0,0;3.14159rad)
  Placement = pos=(0,4.71e-14,-293) rot=(1,0,0;3.14159rad)
  _LinkVersion = 1
  _Parent = -> Constraint019
FEATURE [App::FeaturePython] ElementLink043  label="X-cart-BP-br@HGH20CA-R-Assembly002"  # link proxy (typed FeaturePython)
  LinkTransform = true
  LinkedObject = -> Element041
  Offset = pos=(0,0,0) rot=(0,0,1;4.71239rad)
  Placement = pos=(179.75,-9.02e-14,-113.25) rot=(0,1,0;1.5708rad)
  _LinkVersion = 1
  _Parent = -> Constraint019
FEATURE [App::FeaturePython] Constraint020  label="Attachment-x-cart-bl"  # WARN: FeaturePython — macro-defined, semantics opaque (R4)
  Cascade = false
  Disabled = false
  Group = -> [ElementLink044,ElementLink045]
  Multiply = false
  _ConstraintType = 45
  _LinkVersion = 1
  _Parent = -> Constraints
FEATURE [App::FeaturePython] ElementLink044  label="x-cart-bl@Backplate-Assembly"  # link proxy (typed FeaturePython)
  LinkTransform = true
  LinkedObject = -> Element043
  Offset = pos=(0,0,0) rot=(1,0,0;3.14159rad)
  Placement = pos=(0,4.71e-14,-293) rot=(1,0,0;3.14159rad)
  _LinkVersion = 1
  _Parent = -> Constraint020
FEATURE [App::FeaturePython] ElementLink045  label="X-cart-BP-bl@HGH20CA-L-Assembly002"  # link proxy (typed FeaturePython)
  LinkTransform = true
  LinkedObject = -> Element042
  Offset = pos=(0,0,0) rot=(0,0,1;4.71239rad)
  Placement = pos=(113.25,-3.99e-14,-179.75) rot=(0,1,0;1.5708rad)
  _LinkVersion = 1
  _Parent = -> Constraint020
FEATURE [Part::FeaturePython] Element053  label="x-cart-BP-tl@HGH20CA-R-Assembly002"  # link proxy (typed FeaturePython)
  Detach = false
  LinkTransform = true
  LinkedObject = -> Link030 [1.$shim-tr.]
  _LinkVersion = 1
  _Parent = -> Elements
FEATURE [Part::FeaturePython] Element054  label="x-cart-BP-tr@HGH20CA-R-Assembly002"  # link proxy (typed FeaturePython)
  Detach = false
  LinkTransform = true
  LinkedObject = -> Link030 [1.$shim-tr.]
  _LinkVersion = 1
  _Parent = -> Elements
FEATURE [Part::FeaturePython] Element055  label="x-cart-tl@Backplate-Assembly"  # link proxy (typed FeaturePython)
  Detach = false
  LinkTransform = true
  LinkedObject = -> Link [1.$x-cart-tl.]
  _LinkVersion = 1
  _Parent = -> Elements
FEATURE [Part::FeaturePython] Element056  label="x-cart-tr@Backplate-Assembly"  # link proxy (typed FeaturePython)
  Detach = false
  LinkTransform = true
  LinkedObject = -> Link [1.$x-cart-tr.]
  _LinkVersion = 1
  _Parent = -> Elements
FEATURE [App::FeaturePython] Constraint023  label="Attachment-x-cart-tr"  # WARN: FeaturePython — macro-defined, semantics opaque (R4)
  Cascade = false
  Disabled = false
  Group = -> [ElementLink051,ElementLink052]
  Multiply = false
  _ConstraintType = 45
  _LinkVersion = 1
  _Parent = -> Constraints
FEATURE [App::FeaturePython] ElementLink051  label="x-cart-tr@Backplate-Assembly"  # link proxy (typed FeaturePython)
  LinkTransform = true
  LinkedObject = -> Element056
  Offset = pos=(0,0,0) rot=(1,0,0;3.14159rad)
  Placement = pos=(0,-8.1e-15,50.4) rot=(1,0,0;3.14159rad)
  _LinkVersion = 1
  _Parent = -> Constraint023
FEATURE [App::FeaturePython] ElementLink052  label="x-cart-BP-tr@HGH20CA-R-Assembly002"  # link proxy (typed FeaturePython)
  LinkTransform = true
  LinkedObject = -> Element054
  Offset = pos=(0,0,0) rot=(0,0,1;1.5708rad)
  Placement = pos=(58.45,2.7e-15,-8.05) rot=(0,-1,0;1.5708rad)
  _LinkVersion = 1
  _Parent = -> Constraint023
FEATURE [Part::FeaturePython] Element057  label="x-top-rail-side-mate@HGH20CA-R-Assembly001"  # link proxy (typed FeaturePython)
  Detach = false
  LinkTransform = true
  LinkedObject = -> Link031 [1.$side-mate.]
  _LinkVersion = 1
  _Parent = -> Elements
FEATURE [Part::FeaturePython] Element058  label="x-top-rail-top-mate@HGH20CA-R-Assembly001"  # link proxy (typed FeaturePython)
  Detach = false
  LinkTransform = true
  LinkedObject = -> Link031 [1.$top-mate.]
  _LinkVersion = 1
  _Parent = -> Elements
FEATURE [Part::FeaturePython] Element059  label="x-nut-BP-mate@NUT Assembly001"  # link proxy (typed FeaturePython)
  Detach = false
  LinkTransform = true
  LinkedObject = -> Link026 [1.$shim-mate.]
  _LinkVersion = 1
  _Parent = -> Elements
FEATURE [Part::FeaturePython] Element060  label="x-nut-mate@Backplate-Assembly"  # link proxy (typed FeaturePython)
  Detach = false
  LinkTransform = true
  LinkedObject = -> Link [1.$x-nut-mate.]
  _LinkVersion = 1
  _Parent = -> Elements
FEATURE [App::FeaturePython] Constraint025  label="Attachment-X-Nut-shim"  # WARN: FeaturePython — macro-defined, semantics opaque (R4)
  Cascade = false
  Disabled = false
  Group = -> [ElementLink056,ElementLink057]
  Multiply = false
  _ConstraintType = 45
  _LinkVersion = 1
  _Parent = -> Constraints
FEATURE [App::FeaturePython] ElementLink056  label="x-nut-BP-mate@NUT Assembly001"  # link proxy (typed FeaturePython)
  LinkTransform = true
  LinkedObject = -> Element059
  _LinkVersion = 1
  _Parent = -> Constraint025
FEATURE [Part::FeaturePython] Element061  label="X-nut-Axis@NUT Assembly001"  # link proxy (typed FeaturePython)
  Detach = false
  LinkTransform = true
  LinkedObject = -> Link026 [1.$Axis.]
  _LinkVersion = 1
  _Parent = -> Elements
FEATURE [Part::FeaturePython] Element062  label="x-cart-point@HGH20CA-R-Assembly001"  # link proxy (typed FeaturePython)
  Detach = false
  LinkTransform = true
  LinkedObject = -> Link031 [1.$point.]
  _LinkVersion = 1
  _Parent = -> Elements
FEATURE [Part::FeaturePython] Element063  label="bp-mate@Nut-shim-X-Assembly"  # link proxy (typed FeaturePython)
  Detach = false
  LinkTransform = true
  LinkedObject = -> Link027 [1.$bp-mate.]
  _LinkVersion = 1
  _Parent = -> Elements
FEATURE [Part::FeaturePython] Element064  label="nut-mate@Nut-shim-X-Assembly"  # link proxy (typed FeaturePython)
  Detach = false
  LinkTransform = true
  LinkedObject = -> Link027 [1.$nut-mate.]
  _LinkVersion = 1
  _Parent = -> Elements
FEATURE [App::FeaturePython] ElementLink057  label="nut-mate@Nut-shim-X-Assembly"  # link proxy (typed FeaturePython)
  LinkTransform = true
  LinkedObject = -> Element064
  _LinkVersion = 1
  _Parent = -> Constraint025
FEATURE [App::FeaturePython] Constraint026  label="Attachment001"  # WARN: FeaturePython — macro-defined, semantics opaque (R4)
  Cascade = false
  Disabled = false
  Group = -> [ElementLink058,ElementLink059]
  Multiply = false
  _ConstraintType = 45
  _LinkVersion = 1
  _Parent = -> Constraints
FEATURE [App::FeaturePython] ElementLink058  label="bp-mate@Nut-shim-X-Assembly"  # link proxy (typed FeaturePython)
  LinkTransform = true
  LinkedObject = -> Element063
  Offset = pos=(0,0,0) rot=(1,0,0;3.14159rad)
  Placement = pos=(-6,-3.5e-15,0) rot=(0,0,1;3.14159rad)
  _LinkVersion = 1
  _Parent = -> Constraint026
FEATURE [App::FeaturePython] ElementLink059  label="x-nut-mate@Backplate-Assembly"  # link proxy (typed FeaturePython)
  LinkTransform = true
  LinkedObject = -> Element060
  Offset = pos=(0,0,0) rot=(0,0,1;4.71239rad)
  Placement = pos=(-43.65,8.4e-15,-37.65) rot=(0,-1,0;1.5708rad)
  _LinkVersion = 1
  _Parent = -> Constraint026
FEATURE [Part::FeaturePython] _Element  label="x-cart-tl@Backplate-Assembly001"  # link proxy (typed FeaturePython)
  Detach = false
  LinkTransform = true
  LinkedObject = -> Link [1.$x-cart-tl.]
  _LinkVersion = 1
  _Parent = -> Elements
FEATURE [App::FeaturePython] Constraint027  label="Attachment-x-cart-tl"  # WARN: FeaturePython — macro-defined, semantics opaque (R4)
  Cascade = false
  Disabled = false
  Group = -> [ElementLink060,ElementLink061]
  Multiply = false
  _ConstraintType = 45
  _LinkVersion = 1
  _Parent = -> Constraints
FEATURE [App::FeaturePython] ElementLink060  label="x-cart-tl@Backplate-Assembly"  # link proxy (typed FeaturePython)
  LinkTransform = true
  LinkedObject = -> Element055
  Offset = pos=(0,0,0) rot=(1,0,0;3.14159rad)
  Placement = pos=(0,3.1e-15,50.4) rot=(1,0,0;3.14159rad)
  _LinkVersion = 1
  _Parent = -> Constraint027
FEATURE [App::FeaturePython] ElementLink061  label="shim-br@HGH20CA-R-Assembly"  # link proxy (typed FeaturePython)
  LinkTransform = true
  LinkedObject = -> _Element001
  Offset = pos=(0,0,0) rot=(0,0,1;1.5708rad)
  Placement = pos=(-8.05,1.3e-14,58.45) rot=(0,-1,0;1.5708rad)
  _LinkVersion = 1
  _Parent = -> Constraint027
FEATURE [Part::FeaturePython] _Element001  label="shim-br@HGH20CA-R-Assembly"  # link proxy (typed FeaturePython)
  Detach = false
  LinkTransform = true
  LinkedObject = -> Link031 [1.$shim-br.]
  _LinkVersion = 1
  _Parent = -> Elements
FEATURE [Part::FeaturePython] Element065  label="limit-mate@Motor Bracket Assembly"  # link proxy (typed FeaturePython)
  Detach = false
  LinkTransform = true
  LinkedObject = -> Link017 [1.$limit-mate.]
  _LinkVersion = 1
  _Parent = -> Elements
FEATURE [App::FeaturePython] Constraint028  label="Attachment-limit-sensor"  # WARN: FeaturePython — macro-defined, semantics opaque (R4)
  Cascade = false
  Disabled = false
  Group = -> [ElementLink062,ElementLink063]
  Multiply = false
  _ConstraintType = 45
  _LinkVersion = 1
  _Parent = -> Constraints
FEATURE [App::FeaturePython] ElementLink062  label="limit-mate@Motor Bracket Assembly"  # link proxy (typed FeaturePython)
  LinkTransform = true
  LinkedObject = -> Element065
  Offset = pos=(0,0,0) rot=(0,0,1;3.14159rad)
  Placement = pos=(-96,-102.7,-5.68e-14) rot=(0,0,1;3.14159rad)
  _LinkVersion = 1
  _Parent = -> Constraint028
FEATURE [App::FeaturePython] ElementLink063  label="mate l@Limit sensor Assembly"  # link proxy (typed FeaturePython)
  LinkTransform = true
  LinkedObject = -> _Element002
  Offset = pos=(0,0,0) rot=(1,0,0;3.14159rad)
  Placement = pos=(0,-102.7,305) rot=(1,0,0;3.14159rad)
  _LinkVersion = 1
  _Parent = -> Constraint028
FEATURE [Part::FeaturePython] _Element002  label="mate l@Limit sensor Assembly"  # link proxy (typed FeaturePython)
  Detach = false
  LinkTransform = true
  LinkedObject = -> Link032 [1.$mate l.]
  _LinkVersion = 1
  _Parent = -> Elements
---- part Z-carriage.FCStd = doc fcstd_a198156366d7 ----
FCSTD DOCUMENT  (FreeCAD 2021.717R24301 +3842 (Git))
Label: Z-carriage
License: Creative Commons Attribution
LicenseURL: http://creativecommons.org/licenses/by/4.0/
objects: App::FeaturePython×34, Part::FeaturePython×25, App::Link×11
note: 24 computed .brp shape members not serialized (recipe doc carries the construction recipe); baked Part::Feature solids carry a one-line shape summary decoded from their .brp
EXTERNAL_REF file=parts/Spindle.FCStd obj=Assembly001
EXTERNAL_REF file=parts/HGH20CA.FCStd obj=Assembly
EXTERNAL_REF file=parts/HGH20CA.FCStd obj=Assembly001
EXTERNAL_REF file=parts/BallNut.FCStd obj=Assembly
EXTERNAL_REF file=parts/Z axis plates.FCStd obj=Assembly002
EXTERNAL_REF file=parts/Z axis plates.FCStd obj=Assembly001
EXTERNAL_REF file=parts/Z axis plates.FCStd obj=Assembly003
EXTERNAL_REF file=parts/Spindle.FCStd obj=Assembly002

FEATURE [App::Link] Link023  label="Spindle 0.8KW"
  AutoLinkLabel = true
  AutoPlacement = true
  LinkPlacement = pos=(255,-86.85,-102.5) rot=(0,0,-1;3.14159rad)
  LinkedObject = -> <external parts/Spindle.FCStd>#Assembly001
  Placement = pos=(255,-86.85,-102.5) rot=(0,0,-1;3.14159rad)
  SyncGroupVisibility = false
  _LinkVersion = 1
FEATURE [App::Link] Link003  label="HGH20CA-L-B"
  AutoLinkLabel = true
  AutoPlacement = true
  LinkPlacement = pos=(34,-18.45,-40.5) rot=(0,0.707107,-0.707107;3.14159rad)
  LinkedObject = -> <external parts/HGH20CA.FCStd>#Assembly
  Placement = pos=(34,-18.45,-40.5) rot=(0,0.707107,-0.707107;3.14159rad)
  SyncGroupVisibility = false
  _LinkVersion = 1
FEATURE [App::Link] Link004  label="HGH20CA-L-T"
  AutoLinkLabel = true
  AutoPlacement = true
  LinkPlacement = pos=(34,-18.45,40.5) rot=(0,0.707107,-0.707107;3.14159rad)
  LinkedObject = -> <external parts/HGH20CA.FCStd>#Assembly001
  Placement = pos=(34,-18.45,40.5) rot=(0,0.707107,-0.707107;3.14159rad)
  SyncGroupVisibility = false
  _LinkVersion = 1
FEATURE [App::Link] Link010  label="NUT"
  AutoLinkLabel = true
  AutoPlacement = true
  LinkPlacement = pos=(88,-43.45,-28.4) rot=(-1,0,0;1.5708rad)
  LinkedObject = -> <external parts/BallNut.FCStd>#Assembly
  Placement = pos=(88,-43.45,-28.4) rot=(-1,0,0;1.5708rad)
  SyncGroupVisibility = false
  _LinkVersion = 1
FEATURE [App::Link] Link013  label="Shim-L"
  AutoLinkLabel = true
  AutoPlacement = true
  LinkPlacement = pos=(88,-14.3,-9.24e-14) rot=(0,0,1;0rad)
  LinkedObject = -> <external parts/Z axis plates.FCStd>#Assembly002
  Placement = pos=(88,-14.3,-9.24e-14) rot=(0,0,1;0rad)
  SyncGroupVisibility = false
  _LinkVersion = 1
FEATURE [App::Link] Link014  label="Shim-R"
  AutoLinkLabel = true
  AutoPlacement = true
  LinkPlacement = pos=(88,-14.3,-1.705e-13) rot=(0,1,0;3.14159rad)
  LinkedObject = -> <external parts/Z axis plates.FCStd>#Assembly002
  Placement = pos=(88,-14.3,-1.705e-13) rot=(0,1,0;3.14159rad)
  SyncGroupVisibility = false
  _LinkVersion = 1
FEATURE [App::Link] Link015  label="Frontplate"
  AutoLinkLabel = true
  AutoPlacement = true
  LinkedObject = -> <external parts/Z axis plates.FCStd>#Assembly001
  SyncGroupVisibility = false
  _LinkVersion = 1
FEATURE [App::Link] Link016  label="Shim-Nut"
  AutoLinkLabel = true
  AutoPlacement = true
  LinkPlacement = pos=(216,-30.45,7.1e-15) rot=(0,0,1;0rad)
  LinkedObject = -> <external parts/Z axis plates.FCStd>#Assembly003
  Placement = pos=(216,-30.45,7.1e-15) rot=(0,0,1;0rad)
  SyncGroupVisibility = false
  _LinkVersion = 1
FEATURE [App::Link] Link  label="HGH20CA-R-T"
  AutoLinkLabel = true
  AutoPlacement = true
  LinkPlacement = pos=(142,-18.45,40.5) rot=(-1,0,0;4.71239rad)
  LinkedObject = -> Link003
  Placement = pos=(142,-18.45,40.5) rot=(-1,0,0;4.71239rad)
  SyncGroupVisibility = false
  _LinkVersion = 1
FEATURE [App::Link] Link024  label="HGH20CA-R-B"
  AutoLinkLabel = true
  AutoPlacement = true
  LinkPlacement = pos=(142,-18.45,-40.5) rot=(-1,0,0;4.71239rad)
  LinkedObject = -> Link004
  Placement = pos=(142,-18.45,-40.5) rot=(-1,0,0;4.71239rad)
  SyncGroupVisibility = false
  _LinkVersion = 1
FEATURE [App::Link] Link025  label="Makita router"
  AutoLinkLabel = true
  AutoPlacement = true
  LinkPlacement = pos=(-82,48.15,-102.5) rot=(0,0,-1;3.14159rad)
  LinkedObject = -> <external parts/Spindle.FCStd>#Assembly002
  Placement = pos=(-82,48.15,-102.5) rot=(0,0,-1;3.14159rad)
  SyncGroupVisibility = false
  _LinkVersion = 1
FEATURE [Part::FeaturePython] Parts  # WARN: FeaturePython — macro-defined, semantics opaque (R4)
  Group = -> [Link023,Link003,Link004,Link010,Link013,Link014,Link015,Link016,Link,Link024,Link025]
  GroupMode = 0
  _LinkVersion = 1
FEATURE [Part::FeaturePython] Assembly  label="Z carriage Assembly"  # WARN: FeaturePython — macro-defined, semantics opaque (R4)
  AutoRelax = true
  BuildShape = 0
  Freeze = false
  Group = -> [Constraints,Elements,Parts]
  Verbose = false
  _LinkVersion = 1
  _SolverType = 1
  _Version = 1
FEATURE [App::FeaturePython] Constraints  # WARN: FeaturePython — macro-defined, semantics opaque (R4)
  Group = -> [Constraint,Constraint001,Constraint002,Constraint003,Constraint004,Constraint005,Constraint006,Constraint007,Constraint008,Constraint009,Constraint010]
  _LinkVersion = 1
  _Version = 1
FEATURE [App::FeaturePython] Elements  # WARN: FeaturePython — macro-defined, semantics opaque (R4)
  Group = -> [_Element,_Element001,_Element002,_Element003,_Element004,_Element005,_Element006,_Element007,_Element008,_Element009,_Element010,_Element011,_Element012,_Element013,_Element014,_Element015,_Element016,_Element017,_Element018,Element,Element001,Element002,Element003]
  _LinkVersion = 1
FEATURE [App::FeaturePython] Constraint  label="Locked"  # WARN: FeaturePython — macro-defined, semantics opaque (R4)
  Disabled = false
  Group = -> [ElementLink]
  _ConstraintType = 0
  _LinkVersion = 1
  _Parent = -> Constraints
FEATURE [App::FeaturePython] ElementLink  label="shim-t-l@Frontplate-Assembly"  # link proxy (typed FeaturePython)
  LinkTransform = true
  LinkedObject = -> _Element
  _LinkVersion = 1
  _Parent = -> Constraint
FEATURE [Part::FeaturePython] _Element  label="shim-t-l@Frontplate-Assembly"  # link proxy (typed FeaturePython)
  Detach = false
  LinkTransform = true
  LinkedObject = -> Link015 [1.$shim-t-l.]
  _LinkVersion = 1
  _Parent = -> Elements
FEATURE [App::FeaturePython] Constraint001  label="Attachment-shim-left"  # WARN: FeaturePython — macro-defined, semantics opaque (R4)
  Cascade = false
  Disabled = false
  Group = -> [ElementLink001,ElementLink002]
  Multiply = false
  _ConstraintType = 45
  _LinkVersion = 1
  _Parent = -> Constraints
FEATURE [App::FeaturePython] ElementLink001  label="front-tl@Shim-Assembly"  # link proxy (typed FeaturePython)
  LinkTransform = true
  LinkedObject = -> _Element001
  Offset = pos=(0,0,0) rot=(1,0,0;3.14159rad)
  Placement = pos=(0,-128.3,117) rot=(1,0,0;3.14159rad)
  _LinkVersion = 1
  _Parent = -> Constraint001
FEATURE [Part::FeaturePython] _Element001  label="front-tl@Shim-Assembly"  # link proxy (typed FeaturePython)
  Detach = false
  LinkTransform = true
  LinkedObject = -> Link013 [1.$front-tl.]
  _LinkVersion = 1
  _Parent = -> Elements
FEATURE [App::FeaturePython] ElementLink002  label="shim-t-l@Frontplate-Assembly"  # link proxy (typed FeaturePython)
  LinkTransform = true
  LinkedObject = -> _Element
  _LinkVersion = 1
  _Parent = -> Constraint001
FEATURE [Part::FeaturePython] _Element002  label="shim-t-r@Frontplate-Assembly"  # link proxy (typed FeaturePython)
  Detach = false
  LinkTransform = true
  LinkedObject = -> Link015 [1.$shim-t-r.]
  _LinkVersion = 1
  _Parent = -> Elements
FEATURE [Part::FeaturePython] _Element003  label="front-tl@Shim-Assembly001"  # link proxy (typed FeaturePython)
  Detach = false
  LinkTransform = true
  LinkedObject = -> Link014 [1.$front-tl.]
  _LinkVersion = 1
  _Parent = -> Elements
FEATURE [App::FeaturePython] Constraint002  label="Attachment-shim-right"  # WARN: FeaturePython — macro-defined, semantics opaque (R4)
  Cascade = false
  Disabled = false
  Group = -> [ElementLink003,ElementLink004]
  Multiply = false
  _ConstraintType = 45
  _LinkVersion = 1
  _Parent = -> Constraints
FEATURE [App::FeaturePython] ElementLink003  label="front-bl@Shim-Assembly"  # link proxy (typed FeaturePython)
  LinkTransform = true
  LinkedObject = -> _Element004
  Offset = pos=(0,0,0) rot=(1,0,0;3.14159rad)
  Placement = pos=(0,-128.3,117) rot=(1,0,0;3.14159rad)
  _LinkVersion = 1
  _Parent = -> Constraint002
FEATURE [Part::FeaturePython] _Element004  label="front-bl@Shim-Assembly"  # link proxy (typed FeaturePython)
  Detach = false
  LinkTransform = true
  LinkedObject = -> Link014 [1.$front-bl.]
  _LinkVersion = 1
  _Parent = -> Elements
FEATURE [App::FeaturePython] ElementLink004  label="shim-t-r@Frontplate-Assembly"  # link proxy (typed FeaturePython)
  LinkTransform = true
  LinkedObject = -> _Element002
  Offset = pos=(0,0,0) rot=(0,0,1;3.14159rad)
  Placement = pos=(316,1.42e-14,117) rot=(0,1,0;3.14159rad)
  _LinkVersion = 1
  _Parent = -> Constraint002
FEATURE [App::FeaturePython] Constraint003  label="Attachment-shim"  # WARN: FeaturePython — macro-defined, semantics opaque (R4)
  Cascade = false
  Disabled = false
  Group = -> [ElementLink005,ElementLink006]
  Multiply = false
  _ConstraintType = 45
  _LinkVersion = 1
  _Parent = -> Constraints
FEATURE [App::FeaturePython] ElementLink005  label="fp-mate@Nut-shim-Assembly"  # link proxy (typed FeaturePython)
  LinkTransform = true
  LinkedObject = -> _Element005
  _LinkVersion = 1
  _Parent = -> Constraint003
FEATURE [Part::FeaturePython] _Element005  label="fp-mate@Nut-shim-Assembly"  # link proxy (typed FeaturePython)
  Detach = false
  LinkTransform = true
  LinkedObject = -> Link016 [1.$fp-mate.]
  _LinkVersion = 1
  _Parent = -> Elements
FEATURE [App::FeaturePython] ElementLink006  label="shim-nut-mate@Frontplate-Assembly"  # link proxy (typed FeaturePython)
  LinkTransform = true
  LinkedObject = -> _Element006
  _LinkVersion = 1
  _Parent = -> Constraint003
FEATURE [Part::FeaturePython] _Element006  label="shim-nut-mate@Frontplate-Assembly"  # link proxy (typed FeaturePython)
  Detach = false
  LinkTransform = true
  LinkedObject = -> Link015 [1.$shim-nut-mate.]
  _LinkVersion = 1
  _Parent = -> Elements
FEATURE [App::FeaturePython] Constraint004  label="Attachment-nut"  # WARN: FeaturePython — macro-defined, semantics opaque (R4)
  Cascade = false
  Disabled = false
  Group = -> [ElementLink007,ElementLink008]
  Multiply = false
  _ConstraintType = 45
  _LinkVersion = 1
  _Parent = -> Constraints
FEATURE [App::FeaturePython] ElementLink007  label="nut-mate@Nut-shim-Assembly"  # link proxy (typed FeaturePython)
  LinkTransform = true
  LinkedObject = -> _Element007
  _LinkVersion = 1
  _Parent = -> Constraint004
FEATURE [Part::FeaturePython] _Element007  label="nut-mate@Nut-shim-Assembly"  # link proxy (typed FeaturePython)
  Detach = false
  LinkTransform = true
  LinkedObject = -> Link016 [1.$nut-mate.]
  _LinkVersion = 1
  _Parent = -> Elements
FEATURE [App::FeaturePython] ElementLink008  label="shim-mate@NUT Assembly"  # link proxy (typed FeaturePython)
  LinkTransform = true
  LinkedObject = -> _Element008
  _LinkVersion = 1
  _Parent = -> Constraint004
FEATURE [Part::FeaturePython] _Element008  label="shim-mate@NUT Assembly"  # link proxy (typed FeaturePython)
  Detach = false
  LinkTransform = true
  LinkedObject = -> Link010 [1.$shim-mate.]
  _LinkVersion = 1
  _Parent = -> Elements
FEATURE [App::FeaturePython] Constraint005  label="Attachment-spindle"  # WARN: FeaturePython — macro-defined, semantics opaque (R4)
  Cascade = false
  Disabled = false
  Group = -> [ElementLink009,ElementLink010]
  Multiply = false
  _ConstraintType = 45
  _LinkVersion = 1
  _Parent = -> Constraints
FEATURE [App::FeaturePython] ElementLink009  label="FP-mate-tl@0_8KW spindle Assembly"  # link proxy (typed FeaturePython)
  LinkTransform = true
  LinkedObject = -> _Element009
  _LinkVersion = 1
  _Parent = -> Constraint005
FEATURE [Part::FeaturePython] _Element009  label="FP-mate-tl@0_8KW spindle Assembly"  # link proxy (typed FeaturePython)
  Detach = false
  LinkTransform = true
  LinkedObject = -> Link023 [1.$FP-mate-tl.]
  _LinkVersion = 1
  _Parent = -> Elements
FEATURE [App::FeaturePython] ElementLink010  label="spindle-65mm-tl@Frontplate-Assembly"  # link proxy (typed FeaturePython)
  LinkTransform = true
  LinkedObject = -> _Element010
  _LinkVersion = 1
  _Parent = -> Constraint005
FEATURE [Part::FeaturePython] _Element010  label="spindle-65mm-tl@Frontplate-Assembly"  # link proxy (typed FeaturePython)
  Detach = false
  LinkTransform = true
  LinkedObject = -> Link015 [1.$spindle-65mm-tl.]
  _LinkVersion = 1
  _Parent = -> Elements
FEATURE [App::FeaturePython] Constraint006  label="Attachment-cart-tl"  # WARN: FeaturePython — macro-defined, semantics opaque (R4)
  Cascade = false
  Disabled = false
  Group = -> [ElementLink011,ElementLink012]
  Multiply = false
  _ConstraintType = 45
  _LinkVersion = 1
  _Parent = -> Constraints
FEATURE [App::FeaturePython] ElementLink011  label="shim-br@HGH20CA-R-Assembly"  # link proxy (typed FeaturePython)
  LinkTransform = true
  LinkedObject = -> _Element011
  _LinkVersion = 1
  _Parent = -> Constraint006
FEATURE [Part::FeaturePython] _Element011  label="shim-br@HGH20CA-R-Assembly"  # link proxy (typed FeaturePython)
  Detach = false
  LinkTransform = true
  LinkedObject = -> Link004 [1.$shim-br.]
  _LinkVersion = 1
  _Parent = -> Elements
FEATURE [App::FeaturePython] ElementLink012  label="cart-tl@Shim-Assembly"  # link proxy (typed FeaturePython)
  LinkTransform = true
  LinkedObject = -> _Element012
  _LinkVersion = 1
  _Parent = -> Constraint006
FEATURE [Part::FeaturePython] _Element012  label="cart-tl@Shim-Assembly"  # link proxy (typed FeaturePython)
  Detach = false
  LinkTransform = true
  LinkedObject = -> Link013 [1.$cart-tl.]
  _LinkVersion = 1
  _Parent = -> Elements
FEATURE [App::FeaturePython] Constraint007  label="Attachment-cart-bl"  # WARN: FeaturePython — macro-defined, semantics opaque (R4)
  Cascade = false
  Disabled = false
  Group = -> [ElementLink013,ElementLink014]
  Multiply = false
  _ConstraintType = 45
  _LinkVersion = 1
  _Parent = -> Constraints
FEATURE [App::FeaturePython] ElementLink013  label="shim-tr@HGH20CA-L-Assembly"  # link proxy (typed FeaturePython)
  LinkTransform = true
  LinkedObject = -> _Element013
  _LinkVersion = 1
  _Parent = -> Constraint007
FEATURE [Part::FeaturePython] _Element013  label="shim-tr@HGH20CA-L-Assembly"  # link proxy (typed FeaturePython)
  Detach = false
  LinkTransform = true
  LinkedObject = -> Link003 [1.$shim-tr.]
  _LinkVersion = 1
  _Parent = -> Elements
FEATURE [App::FeaturePython] ElementLink014  label="cart-bl@Shim-Assembly"  # link proxy (typed FeaturePython)
  LinkTransform = true
  LinkedObject = -> _Element014
  _LinkVersion = 1
  _Parent = -> Constraint007
FEATURE [Part::FeaturePython] _Element014  label="cart-bl@Shim-Assembly"  # link proxy (typed FeaturePython)
  Detach = false
  LinkTransform = true
  LinkedObject = -> Link013 [1.$cart-bl.]
  _LinkVersion = 1
  _Parent = -> Elements
FEATURE [Part::FeaturePython] _Element015  label="shim-tr@HGH20CA-L-Assembly001"  # link proxy (typed FeaturePython)
  Detach = false
  LinkTransform = true
  LinkedObject = -> Link [1.$shim-tr.]
  _LinkVersion = 1
  _Parent = -> Elements
FEATURE [App::FeaturePython] Constraint008  label="Attachment-cart-tr"  # WARN: FeaturePython — macro-defined, semantics opaque (R4)
  Cascade = false
  Disabled = false
  Group = -> [ElementLink015,ElementLink016]
  Multiply = false
  _ConstraintType = 45
  _LinkVersion = 1
  _Parent = -> Constraints
FEATURE [App::FeaturePython] ElementLink015  label="shim-tr@HGH20CA-L-Assembly001"  # link proxy (typed FeaturePython)
  LinkTransform = true
  LinkedObject = -> _Element015
  _LinkVersion = 1
  _Parent = -> Constraint008
FEATURE [App::FeaturePython] ElementLink016  label="cart-bl@Shim-Assembly001"  # link proxy (typed FeaturePython)
  LinkTransform = true
  LinkedObject = -> _Element016
  _LinkVersion = 1
  _Parent = -> Constraint008
FEATURE [Part::FeaturePython] _Element016  label="cart-bl@Shim-Assembly001"  # link proxy (typed FeaturePython)
  Detach = false
  LinkTransform = true
  LinkedObject = -> Link014 [1.$cart-bl.]
  _LinkVersion = 1
  _Parent = -> Elements
FEATURE [App::FeaturePython] Constraint009  label="Attachment-cart-br"  # WARN: FeaturePython — macro-defined, semantics opaque (R4)
  Cascade = false
  Disabled = false
  Group = -> [ElementLink017,ElementLink018]
  Multiply = false
  _ConstraintType = 45
  _LinkVersion = 1
  _Parent = -> Constraints
FEATURE [App::FeaturePython] ElementLink017  label="cart-tl@Shim-Assembly001"  # link proxy (typed FeaturePython)
  LinkTransform = true
  LinkedObject = -> _Element017
  _LinkVersion = 1
  _Parent = -> Constraint009
FEATURE [Part::FeaturePython] _Element017  label="cart-tl@Shim-Assembly001"  # link proxy (typed FeaturePython)
  Detach = false
  LinkTransform = true
  LinkedObject = -> Link014 [1.$cart-tl.]
  _LinkVersion = 1
  _Parent = -> Elements
FEATURE [App::FeaturePython] ElementLink018  label="shim-br@HGH20CA-R-Assembly001"  # link proxy (typed FeaturePython)
  LinkTransform = true
  LinkedObject = -> _Element018
  _LinkVersion = 1
  _Parent = -> Constraint009
FEATURE [Part::FeaturePython] _Element018  label="shim-br@HGH20CA-R-Assembly001"  # link proxy (typed FeaturePython)
  Detach = false
  LinkTransform = true
  LinkedObject = -> Link024 [1.$shim-br.]
  _LinkVersion = 1
  _Parent = -> Elements
FEATURE [Part::FeaturePython] Element  label="point@HGH20CA-R-Assembly"  # link proxy (typed FeaturePython)
  Detach = false
  LinkTransform = true
  LinkedObject = -> Link024 [1.$point.]
  _LinkVersion = 1
  _Parent = -> Elements
FEATURE [Part::FeaturePython] Element001  label="top-mate@HGH20CA-R-Assembly"  # link proxy (typed FeaturePython)
  Detach = false
  LinkTransform = true
  LinkedObject = -> Link024 [1.$top-mate.]
  _LinkVersion = 1
  _Parent = -> Elements
FEATURE [Part::FeaturePython] Element002  label="side-mate@HGH20CA-R-Assembly"  # link proxy (typed FeaturePython)
  Detach = false
  LinkTransform = true
  LinkedObject = -> Link024 [1.$side-mate.]
  _LinkVersion = 1
  _Parent = -> Elements
FEATURE [Part::FeaturePython] Element003  label="FP-mate@Makita router Assembly"  # link proxy (typed FeaturePython)
  Detach = false
  LinkTransform = true
  LinkedObject = -> Link025 [1.$FP-mate.]
  _LinkVersion = 1
  _Parent = -> Elements
FEATURE [App::FeaturePython] Constraint010  label="Attachment"  # WARN: FeaturePython — macro-defined, semantics opaque (R4)
  Cascade = false
  Disabled = false
  Group = -> [ElementLink019,ElementLink020]
  Multiply = false
  _ConstraintType = 45
  _LinkVersion = 1
  _Parent = -> Constraints
FEATURE [App::FeaturePython] ElementLink019  label="spindle-65mm-tl@Frontplate-Assembly"  # link proxy (typed FeaturePython)
  LinkTransform = true
  LinkedObject = -> _Element010
  _LinkVersion = 1
  _Parent = -> Constraint010
FEATURE [App::FeaturePython] ElementLink020  label="FP-mate@Makita router Assembly"  # link proxy (typed FeaturePython)
  LinkTransform = true
  LinkedObject = -> Element003
  _LinkVersion = 1
  _Parent = -> Constraint010
